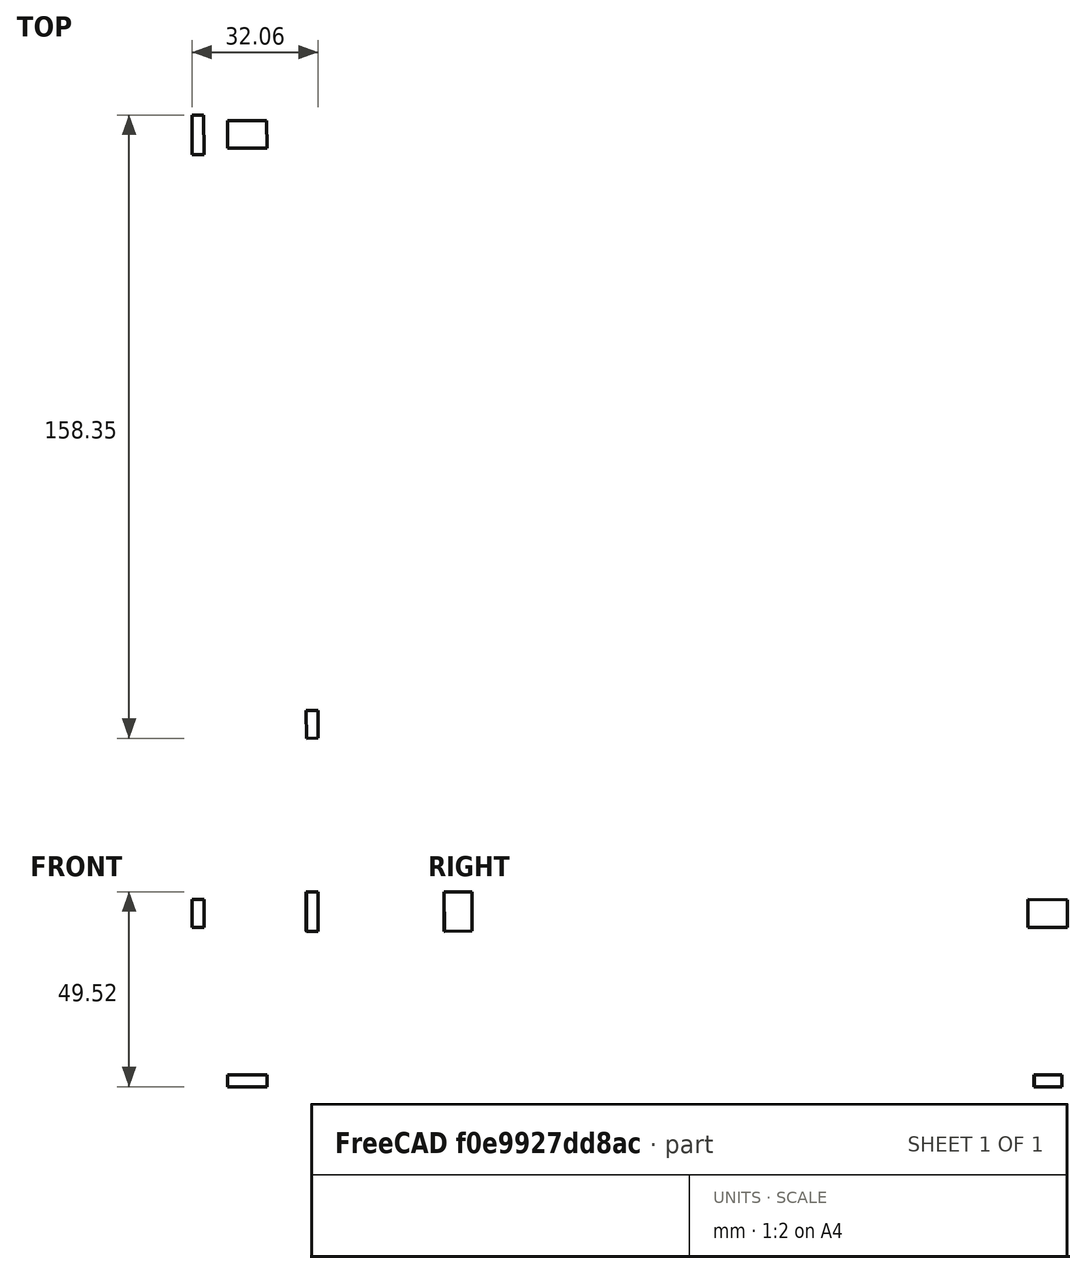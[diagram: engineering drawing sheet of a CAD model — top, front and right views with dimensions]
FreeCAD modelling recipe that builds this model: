
FCSTD DOCUMENT  (FreeCAD 2024.1R35694 (Git))
Label: 3axis_robot_rotation
License: All rights reserved
LicenseURL: https://en.wikipedia.org/wiki/All_rights_reserved
objects: App::FeaturePython×17, App::Link×14, Part::FeaturePython×3, Assembly::JointGroup×1, Assembly::AssemblyObject×1
note: 3 computed .brp shape members not serialized (recipe doc carries the construction recipe); baked Part::Feature solids carry a one-line shape summary decoded from their .brp
EXTERNAL_REF file=base.FCStd obj=Part
EXTERNAL_REF file=nema17-48.FCStd obj=Part
EXTERNAL_REF file=arm0.FCStd obj=Part
EXTERNAL_REF file=arm1.FCStd obj=Part
EXTERNAL_REF file=bearing625.FCStd obj=Part
EXTERNAL_REF file=shaft0.FCStd obj=Part
EXTERNAL_REF file=shaft1.FCStd obj=Part
EXTERNAL_REF file=bevel_gear.FCStd obj=Part
EXTERNAL_REF file=arm2.FCStd obj=Part

FEATURE [App::Link] base  label="base 🔒"
  LinkedObject = -> <external base.FCStd>#Part
FEATURE [App::Link] nema17_48
  LinkPlacement = pos=(0,0,2) rot=(0,0,1;0rad)
  LinkedObject = -> <external nema17-48.FCStd>#Part
  Placement = pos=(0,0,2) rot=(0,0,1;0rad)
FEATURE [App::Link] arm0
  LinkPlacement = pos=(-1.3e-15,-1e-16,6) rot=(0,0,1;0.006716rad)
  LinkedObject = -> <external arm0.FCStd>#Part
  Placement = pos=(-1.3e-15,-1e-16,6) rot=(0,0,1;0.006716rad)
FEATURE [App::Link] nema17_049  label="nema17_48_1"
  LinkPlacement = pos=(12.9997,0.0873078,70) rot=(0.574765,0.578638,-0.578638;4.18491rad)
  LinkedObject = -> <external nema17-48.FCStd>#Part
  Placement = pos=(12.9997,0.0873078,70) rot=(0.574765,0.578638,-0.578638;4.18491rad)
FEATURE [App::Link] arm1
  LinkPlacement = pos=(8.9998,0.0604439,70) rot=(-0.575429,-0.577323,0.579293;2.10026rad)
  LinkedObject = -> <external arm1.FCStd>#Part
  Placement = pos=(8.9998,0.0604439,70) rot=(-0.575429,-0.577323,0.579293;2.10026rad)
FEATURE [App::Link] nema17_050  label="nema17_48_2"
  LinkPlacement = pos=(-23.0868,12.8452,69.9554) rot=(0.575397,0.579274,-0.577374;2.08853rad)
  LinkedObject = -> <external nema17-48.FCStd>#Part
  Placement = pos=(-23.0868,12.8452,69.9554) rot=(0.575397,0.579274,-0.577374;2.08853rad)
FEATURE [App::Link] b625
  LinkPlacement = pos=(5.0073,-149.969,70.5145) rot=(-0.45482,-0.001527,0.890582;0.007541rad)
  LinkedObject = -> <external bearing625.FCStd>#Part
  Placement = pos=(5.0073,-149.969,70.5145) rot=(-0.45482,-0.001527,0.890582;0.007541rad)
FEATURE [App::Link] b626  label="b625_2"
  LinkPlacement = pos=(0.00741419,-150.002,70.5145) rot=(0.00237,-0.705891,0.708316;3.14635rad)
  LinkedObject = -> <external bearing625.FCStd>#Part
  Placement = pos=(0.00741419,-150.002,70.5145) rot=(0.00237,-0.705891,0.708316;3.14635rad)
FEATURE [App::Link] b627  label="b625_3"
  LinkPlacement = pos=(-22.16,-125.151,70.4287) rot=(-0.001715,-0.001727,-0.999997;1.56408rad)
  LinkedObject = -> <external bearing625.FCStd>#Part
  Placement = pos=(-22.16,-125.151,70.4287) rot=(-0.001715,-0.001727,-0.999997;1.56408rad)
FEATURE [App::Link] shaft001  label="shaft0"
  LinkPlacement = pos=(-22.066,-139.151,70.4768) rot=(0.582023,-0.576162,0.573835;4.18633rad)
  LinkedObject = -> <external shaft0.FCStd>#Part
  Placement = pos=(-22.066,-139.151,70.4768) rot=(0.582023,-0.576162,0.573835;4.18633rad)
FEATURE [App::Link] shaft1
  LinkPlacement = pos=(-3.9925,-150.029,70.5145) rot=(-0.002376,0.707591,-0.706618;3.13685rad)
  LinkedObject = -> <external shaft1.FCStd>#Part
  Placement = pos=(-3.9925,-150.029,70.5145) rot=(-0.002376,0.707591,-0.706618;3.13685rad)
FEATURE [App::Link] bevel_gear
  LinkPlacement = pos=(-3.9925,-150.029,70.5145) rot=(-0.707102,-0.002861,0.707106;3.14537rad)
  LinkedObject = -> <external bevel_gear.FCStd>#Part
  Placement = pos=(-3.9925,-150.029,70.5145) rot=(-0.707102,-0.002861,0.707106;3.14537rad)
FEATURE [App::Link] bevel_gear001
  LinkPlacement = pos=(-22.113,-132.151,70.4528) rot=(0.5725,0.580698,-0.578822;2.09287rad)
  LinkedObject = -> <external bevel_gear.FCStd>#Part
  Placement = pos=(-22.113,-132.151,70.4528) rot=(0.5725,0.580698,-0.578822;2.09287rad)
FEATURE [App::Link] arm2
  LinkPlacement = pos=(15.0071,-149.902,70.5145) rot=(-0.707102,-0.002861,0.707106;3.14537rad)
  LinkedObject = -> <external arm2.FCStd>#Part
  Placement = pos=(15.0071,-149.902,70.5145) rot=(-0.707102,-0.002861,0.707106;3.14537rad)
FEATURE [App::FeaturePython] GroundedJoint  # Assembly grounded joint (typed FeaturePython)
  ObjectToGround = -> base
FEATURE [App::FeaturePython] Fixed  # Assembly joint (typed FeaturePython)
  Activated = true
  Detach1 = false
  Detach2 = false
  Distance = 0
  Element1 = Edge11
  Element2 = Edge75
  JointType = 0 (Fixed)
  Object1 = Body
  Object2 = Body
  Offset = (0,0,0)
  Part1 = -> nema17_48
  Part2 = -> base
  Placement1 = pos=(0,0,48) rot=(0,0,1;0rad)
  Rotation = 0
  Vertex1 = Edge11
  Vertex2 = Edge75
FEATURE [App::FeaturePython] Revolute  # Assembly joint (typed FeaturePython)
  Activated = true
  Detach1 = false
  Detach2 = false
  Distance = 0
  Element1 = Face22
  Element2 = Face23
  JointType = 1 (Revolute)
  Object1 = Body
  Object2 = Body
  Offset = (0,0,0)
  Part1 = -> arm0
  Part2 = -> nema17_48
  Placement1 = pos=(4e-16,-1e-16,18) rot=(0,0,1;0rad)
  Placement2 = pos=(-9e-16,-2e-16,72) rot=(0,0,1;0rad)
  Rotation = 0
  Vertex1 = Face22
  Vertex2 = Face23
FEATURE [App::FeaturePython] Fixed001  # Assembly joint (typed FeaturePython)
  Activated = true
  Detach1 = false
  Detach2 = false
  Distance = 0
  Element1 = Edge34
  Element2 = Edge11
  JointType = 0 (Fixed)
  Object1 = Body
  Object2 = Body
  Offset = (0,0,0)
  Part1 = -> arm0
  Part2 = -> nema17_049
  Placement1 = pos=(15,5.2e-15,64) rot=(0.57735,0.57735,0.57735;2.0944rad)
  Placement2 = pos=(0,0,48) rot=(0,0,1;0rad)
  Rotation = 0
  Vertex1 = Edge34
  Vertex2 = Edge11
FEATURE [App::FeaturePython] Revolute001  # Assembly joint (typed FeaturePython)
  Activated = true
  Detach1 = false
  Detach2 = false
  Distance = 0
  Element1 = Face27
  Element2 = Face23
  JointType = 1 (Revolute)
  Object1 = Body001
  Object2 = Body
  Offset = (0,0,0)
  Part1 = -> arm1
  Part2 = -> nema17_049
  Placement1 = pos=(4e-16,-1e-16,18) rot=(0,0,1;0rad)
  Placement2 = pos=(-9e-16,-2e-16,72) rot=(0,0,1;0rad)
  Rotation = 0
  Vertex1 = Face27
  Vertex2 = Face23
FEATURE [App::FeaturePython] Fixed002  # Assembly joint (typed FeaturePython)
  Activated = true
  Detach1 = false
  Detach2 = false
  Distance = 0
  Element1 = Edge25
  Element2 = Edge11
  JointType = 0 (Fixed)
  Object1 = Body001
  Object2 = Body
  Offset = (0,0,0)
  Part1 = -> arm1
  Part2 = -> nema17_050
  Placement1 = pos=(15,-1.2e-15,32) rot=(0.57735,0.57735,0.57735;2.0944rad)
  Placement2 = pos=(0,0,48) rot=(0,0,1;0rad)
  Rotation = 0
  Vertex1 = Edge25
  Vertex2 = Edge11
FEATURE [App::FeaturePython] Fixed003  # Assembly joint (typed FeaturePython)
  Activated = true
  Detach1 = false
  Detach2 = false
  Distance = 0
  Element1 = Edge2
  Element2 = Edge81
  JointType = 0 (Fixed)
  Object1 = Body
  Object2 = Body001
  Offset = (0,0,0)
  Part1 = -> b627
  Part2 = -> arm1
  Placement2 = pos=(-125,-1.2e-15,32) rot=(0.57735,0.57735,0.57735;2.0944rad)
  Rotation = 0
  Vertex1 = Edge2
  Vertex2 = Edge81
FEATURE [App::FeaturePython] Fixed004  # Assembly joint (typed FeaturePython)
  Activated = true
  Detach1 = false
  Detach2 = false
  Distance = 0
  Element1 = Edge2
  Element2 = Edge52
  JointType = 0 (Fixed)
  Object1 = Body
  Object2 = Body001
  Offset = (0,0,0)
  Part1 = -> b626
  Part2 = -> arm1
  Placement2 = pos=(-150,-4.1e-15,10) rot=(1,0,0;3.14159rad)
  Rotation = 0
  Vertex1 = Edge2
  Vertex2 = Edge52
FEATURE [App::FeaturePython] Fixed005  # Assembly joint (typed FeaturePython)
  Activated = true
  Detach1 = false
  Detach2 = false
  Distance = 0
  Element1 = Edge3
  Element2 = Edge17
  JointType = 0 (Fixed)
  Object1 = Body
  Object2 = Body001
  Offset = (0,0,0)
  Part1 = -> b625
  Part2 = -> arm1
  Placement1 = pos=(0,0,5) rot=(0,0,1;0rad)
  Placement2 = pos=(-150,-4.1e-15,0) rot=(1,0,0;3.14159rad)
  Rotation = 0
  Vertex1 = Edge3
  Vertex2 = Edge17
FEATURE [App::FeaturePython] Revolute002  # Assembly joint (typed FeaturePython)
  Activated = true
  Detach1 = false
  Detach2 = false
  Distance = 0
  Element1 = Face11
  Element2 = Face23
  JointType = 1 (Revolute)
  Object1 = Body
  Object2 = Body
  Offset = (0,0,0)
  Part1 = -> shaft001
  Part2 = -> nema17_050
  Placement1 = pos=(-130,0,0) rot=(0.57735,0.57735,0.57735;2.0944rad)
  Placement2 = pos=(0,0,72) rot=(0,0,1;0rad)
  Rotation = 0
  Vertex1 = Edge1
  Vertex2 = Edge1
FEATURE [App::FeaturePython] Revolute003  # Assembly joint (typed FeaturePython)
  Activated = true
  Detach1 = false
  Detach2 = false
  Distance = 0
  Element1 = Edge2
  Element2 = Edge5
  JointType = 1 (Revolute)
  Object1 = Body
  Object2 = Body
  Offset = (0,0,0)
  Part1 = -> shaft1
  Part2 = -> b626
  Placement1 = pos=(-4,0,0) rot=(0.57735,0.57735,0.57735;2.0944rad)
  Rotation = 0
  Vertex1 = Edge2
  Vertex2 = Edge5
FEATURE [App::FeaturePython] Fixed006  # Assembly joint (typed FeaturePython)
  Activated = true
  Detach1 = false
  Detach2 = false
  Distance = 0
  Element1 = Face4
  Element2 = Edge3
  JointType = 0 (Fixed)
  Object1 = Body
  Object2 = Body
  Offset = (0,0,0)
  Part1 = -> shaft1
  Part2 = -> arm2
  Placement1 = pos=(-19,0,0) rot=(0.57735,0.57735,0.57735;2.0944rad)
  Rotation = 0
  Vertex1 = Edge1
  Vertex2 = Edge3
FEATURE [App::FeaturePython] Fixed007  # Assembly joint (typed FeaturePython)
  Activated = true
  Detach1 = false
  Detach2 = false
  Distance = 0
  Element2 = Edge5
  JointType = 0 (Fixed)
  Object1 = Body
  Object2 = Body
  Offset = (0,0,0)
  Part1 = -> bevel_gear
  Part2 = -> shaft1
  Placement2 = pos=(0,0,0) rot=(0.57735,0.57735,0.57735;2.0944rad)
  Rotation = 0
  Vertex2 = Edge5
FEATURE [App::FeaturePython] Fixed008  # Assembly joint (typed FeaturePython)
  Activated = true
  Detach1 = false
  Detach2 = false
  Distance = 0
  Element2 = Edge9
  JointType = 0 (Fixed)
  Object1 = Body
  Object2 = Body
  Offset = (0,0,0)
  Part1 = -> bevel_gear001
  Part2 = -> shaft001
  Placement2 = pos=(-7,0,0) rot=(-0.57735,-0.57735,0.57735;2.0944rad)
  Rotation = 0
  Vertex2 = Edge9
FEATURE [Part::FeaturePython] MotorObserver0  # WARN: FeaturePython — macro-defined, semantics opaque (R4)
  Enabled = true
  Placement = pos=(-1.5e-15,-1e-16,27.5) rot=(0,0,1;0.006716rad)
  SupportObject = -> nema17_48
  TransfAngle = 0
FEATURE [Part::FeaturePython] MotorObserver1  # WARN: FeaturePython — macro-defined, semantics opaque (R4)
  Enabled = true
  Placement = pos=(-12.4997,-0.0839498,70) rot=(-0.575429,-0.577323,0.579293;2.10026rad)
  SupportObject = -> nema17_049
  TransfAngle = 0
FEATURE [Part::FeaturePython] MotorObserver2  # WARN: FeaturePython — macro-defined, semantics opaque (R4)
  Enabled = true
  Placement = pos=(16.507,-149.892,70.5145) rot=(-0.00267,0.999988,0.004046;1.57081rad)
  SupportObject = -> arm1
  TransfAngle = 0
FEATURE [App::FeaturePython] Fixed009  # Assembly joint (typed FeaturePython)
  Activated = true
  Detach1 = false
  Detach2 = false
  Distance = 0
  Element1 = Face5
  Element2 = Edge4
  JointType = 0 (Fixed)
  Object1 = MotorObserver0
  Object2 = Body
  Offset = (0,0,0)
  Part1 = -> MotorObserver0
  Part2 = -> arm0
  Placement1 = pos=(1e-16,0,-1.5) rot=(0,0,1;0rad)
  Placement2 = pos=(0,0,20) rot=(0,0,1;0rad)
  Rotation = 0
  Vertex1 = Face5
  Vertex2 = Edge4
FEATURE [App::FeaturePython] Fixed010  # Assembly joint (typed FeaturePython)
  Activated = true
  Detach1 = false
  Detach2 = false
  Distance = 0
  Element1 = Face5
  Element2 = Edge47
  JointType = 0 (Fixed)
  Object1 = MotorObserver1
  Object2 = Body001
  Offset = (0,0,0)
  Part1 = -> MotorObserver1
  Part2 = -> arm1
  Placement1 = pos=(2e-16,0,-1.5) rot=(0,0,1;0rad)
  Placement2 = pos=(0,0,20) rot=(0,0,1;0rad)
  Rotation = 0
  Vertex1 = Face5
  Vertex2 = Edge47
FEATURE [App::FeaturePython] Fixed011  # Assembly joint (typed FeaturePython)
  Activated = true
  Detach1 = false
  Detach2 = false
  Distance = 0
  Element1 = Face5
  Element2 = Edge3
  JointType = 0 (Fixed)
  Object1 = MotorObserver2
  Object2 = Body
  Offset = (0,0,0)
  Part1 = -> MotorObserver2
  Part2 = -> arm2
  Placement1 = pos=(0,2.84e-14,-1.5) rot=(0,0,1;0rad)
  Rotation = 0
  Vertex1 = Face5
  Vertex2 = Edge3
FEATURE [Assembly::JointGroup] Joints
  Group = -> [GroundedJoint,Fixed,Revolute,Fixed001,Revolute001,Fixed002,Fixed003,Fixed004,Fixed005,Revolute002,Revolute003,Fixed006,Fixed007,Fixed008,Fixed009,Fixed010,Fixed011]
FEATURE [Assembly::AssemblyObject] Assembly  label="3axis_robot"
  Group = -> [Joints,base,nema17_48,arm0,nema17_049,arm1,nema17_050,b625,b626,b627,shaft001,shaft1,bevel_gear,bevel_gear001,arm2,GroundedJoint,Fixed,Revolute,Fixed001,Revolute001,Fixed002,Fixed003,Fixed004,Fixed005,Revolute002,Revolute003,Fixed006,Fixed007,Fixed008,MotorObserver0,MotorObserver1,MotorObserver2,Fixed009,Fixed010,Fixed011]
  Origin = -> Origin
  Type = Assembly

RESOLVED EXTERNAL PARTS (link-assembly join: the EXTERNAL_REF files above that resolve inside this repo's crawl, each included once):
---- part arm0.FCStd = doc fcstd_8672410c447e ----
FCSTD DOCUMENT  (FreeCAD 2024.1R35694 (Git))
Label: arm0
License: All rights reserved
LicenseURL: https://en.wikipedia.org/wiki/All_rights_reserved
objects: Sketcher::SketchObject×11, PartDesign::Pad×6, PartDesign::Hole×3, PartDesign::Body×2, PartDesign::Pocket×2, PartDesign::Fillet×1, App::Part×1
note: 37 computed .brp shape members not serialized (recipe doc carries the construction recipe); baked Part::Feature solids carry a one-line shape summary decoded from their .brp

FEATURE [Sketcher::SketchObject] Sketch
  FullyConstrained = true
  MapMode = 5
  Support = -> [XY_Plane001]
  sketch-geometry (5):
    g0: Circle CenterX=0 CenterY=0 CenterZ=0 NormalX=0 NormalY=0 NormalZ=1 AngleXU=0 Radius=2.5
    g1: ArcOfCircle CenterX=0 CenterY=0 CenterZ=0 NormalX=0 NormalY=0 NormalZ=1 AngleXU=0 Radius=7.5 StartAngle=1.5708 EndAngle=4.71239
    g2: LineSegment StartX=-1.2e-15 StartY=7.5 StartZ=0 EndX=15 EndY=7.5 EndZ=0
    g3: LineSegment StartX=15 StartY=7.5 StartZ=0 EndX=15 EndY=-7.5 EndZ=0
    g4: LineSegment StartX=15 StartY=-7.5 StartZ=0 EndX=1.8e-15 EndY=-7.5 EndZ=0
  constraints (12):
    c: Coincident(g0,g-1)
    c: Coincident(g1,g0)
    c: Diameter(g0) = 5
    c: Diameter(g1) = 15
    c: Horizontal(g2)
    c: Coincident(g2,g3)
    c: Vertical(g3)
    c: Coincident(g3,g4)
    c: Horizontal(g4)
    c: Tangent(g1,g4) = 1.5708
    c: Tangent(g1,g2) = 1.5708
    c: DistanceX(g2,g2) = 15
FEATURE [PartDesign::Pad] Pad
  Direction = (0,0,1)
  Length = 20
  Length2 = 10
  Profile = -> Sketch
  ReferenceAxis = -> Sketch [N_Axis]
  Refine = true
  Type = 0
FEATURE [Sketcher::SketchObject] Sketch001
  ExternalGeometry = -> [Pad]
  FullyConstrained = true
  MapMode = 5
  Placement = pos=(15,0,0) rot=(0.57735,0.57735,0.57735;2.0944rad)
  Support = -> [Pad]
  sketch-geometry (8):
    g0: LineSegment StartX=-7.5 StartY=0 StartZ=0 EndX=-21 EndY=43 EndZ=0
    g1: LineSegment StartX=-21 StartY=43 StartZ=0 EndX=-21 EndY=85 EndZ=0
    g2: LineSegment StartX=-21 StartY=85 StartZ=0 EndX=21 EndY=85 EndZ=0
    g3: LineSegment StartX=21 StartY=85 StartZ=0 EndX=21 EndY=43 EndZ=0
    g4: LineSegment StartX=21 StartY=43 StartZ=0 EndX=7.5 EndY=0 EndZ=0
    g5: LineSegment StartX=7.5 StartY=0 StartZ=0 EndX=-7.5 EndY=0 EndZ=0
    g6: GeomPoint X=5.2e-15 Y=64 Z=0
    g7: Circle CenterX=5.2e-15 CenterY=64 CenterZ=0 NormalX=0 NormalY=0 NormalZ=1 AngleXU=0 Radius=11.25
  constraints (18):
    c: PointOnObject(g0,g-1)
    c: Coincident(g0,g1)
    c: Vertical(g1)
    c: Coincident(g1,g2)
    c: Coincident(g2,g3)
    c: Coincident(g3,g4)
    c: Coincident(g4,g5)
    c: Coincident(g5,g0)
    c: Symmetric(g0,g3,g-2)
    c: Symmetric(g1,g2,g-2)
    c: DistanceX(g2,g2) = 42
    c: DistanceY(g3,g3) = 42
    c: Symmetric(g0,g4,g-2)
    c: DistanceX(g5,g5) = 15
    c: Symmetric(g1,g3,g6)
    c: Coincident(g7,g6)
    c: Diameter(g7) = 22.5
    c: DistanceY(g-1,g3) = 43
FEATURE [PartDesign::Pad] Pad001
  BaseFeature = -> Pad
  Direction = (1,0,0)
  Length = 4
  Length2 = 10
  Profile = -> Sketch001
  ReferenceAxis = -> Sketch001 [N_Axis]
  Refine = true
  Reversed = true
  Type = 0
FEATURE [Sketcher::SketchObject] Sketch003
  ExternalGeometry = -> [Pad001]
  FullyConstrained = true
  MapMode = 5
  Placement = pos=(11,0,0) rot=(0.57735,-0.57735,-0.57735;2.0944rad)
  Support = -> [Pad001]
  sketch-geometry (5):
    g0: Circle CenterX=15.5 CenterY=79.5 CenterZ=0 NormalX=0 NormalY=0 NormalZ=1 AngleXU=0 Radius=1.5
    g1: LineSegment StartX=-5.2e-15 StartY=64 StartZ=0 EndX=11.25 EndY=64 EndZ=0
    g2: Circle CenterX=-15.5 CenterY=79.5 CenterZ=0 NormalX=0 NormalY=0 NormalZ=1 AngleXU=0 Radius=1.5
    g3: Circle CenterX=15.5 CenterY=48.5 CenterZ=0 NormalX=0 NormalY=0 NormalZ=1 AngleXU=0 Radius=1.5
    g4: Circle CenterX=-15.5 CenterY=48.5 CenterZ=0 NormalX=0 NormalY=0 NormalZ=1 AngleXU=0 Radius=1.5
  constraints (12):
    c: DistanceY(g-3,g0) = 15.5
    c: DistanceX(g-3,g0) = 15.5
    c: Diameter(g0) = 3
    c: Coincident(g1,g-3)
    c: Horizontal(g1)
    c: PointOnObject(g1,g-3)
    c: Diameter(g2) = 3
    c: Diameter(g3) = 3
    c: Diameter(g4) = 3
    c: Symmetric(g2,g0,g-2)
    c: Symmetric(g4,g3,g-2)
    c: Symmetric(g3,g0,g1)
FEATURE [PartDesign::Hole] Hole
  BaseFeature = -> Pad001
  CustomThreadClearance = 0
  Depth = 25
  DepthType = 0
  Diameter = 3.4
  DrillForDepth = false
  DrillPoint = 1
  DrillPointAngle = 118
  HoleCutCountersinkAngle = 90
  HoleCutCustomValues = false
  HoleCutDepth = 2
  HoleCutDiameter = 6.1
  HoleCutType = 1
  ModelThread = false
  Profile = -> Sketch003
  Refine = true
  Tapered = false
  TaperedAngle = 90
  ThreadClass = 0
  ThreadDepth = 25
  ThreadDepthType = 0
  ThreadDirection = 0
  ThreadFit = 0
  ThreadSize = 9
  ThreadType = 1
  Threaded = false
  UseCustomThreadClearance = false
FEATURE [Sketcher::SketchObject] Sketch004
  ExternalGeometry = -> [Hole]
  FullyConstrained = true
  MapMode = 5
  Placement = pos=(0,0,20) rot=(0,0,1;0rad)
  Support = -> [Hole]
  sketch-geometry (1):
    g0: Circle CenterX=0 CenterY=0 CenterZ=0 NormalX=0 NormalY=0 NormalZ=1 AngleXU=0 Radius=2.5
  constraints (2):
    c: Coincident(g0,g-3)
    c: Equal(g0,g-3)
FEATURE [PartDesign::Pad] Pad002
  BaseFeature = -> Hole
  Direction = (0,0,1)
  Length = 2
  Length2 = 10
  Profile = -> Sketch004
  ReferenceAxis = -> Sketch004 [N_Axis]
  Refine = true
  Reversed = true
  Type = 0
FEATURE [PartDesign::Body] Body  label="arm0-skel"
  Group = -> [Sketch,Pad,Sketch001,Pad001,Sketch003,Hole,Sketch004,Pad002]
  Origin = -> Origin001
  Tip = -> Pad002
FEATURE [Sketcher::SketchObject] Sketch008
  FullyConstrained = true
  MapMode = 5
  Support = -> [XY_Plane002]
  sketch-geometry (5):
    g0: Circle CenterX=0 CenterY=0 CenterZ=0 NormalX=0 NormalY=0 NormalZ=1 AngleXU=0 Radius=2.5
    g1: ArcOfCircle CenterX=0 CenterY=0 CenterZ=0 NormalX=0 NormalY=0 NormalZ=1 AngleXU=0 Radius=7.5 StartAngle=1.5708 EndAngle=4.71239
    g2: LineSegment StartX=-1.2e-15 StartY=7.5 StartZ=0 EndX=15 EndY=7.5 EndZ=0
    g3: LineSegment StartX=15 StartY=7.5 StartZ=0 EndX=15 EndY=-7.5 EndZ=0
    g4: LineSegment StartX=15 StartY=-7.5 StartZ=0 EndX=1.8e-15 EndY=-7.5 EndZ=0
  constraints (12):
    c: Coincident(g0,g-1)
    c: Coincident(g1,g0)
    c: Diameter(g0) = 5
    c: Diameter(g1) = 15
    c: Horizontal(g2)
    c: Coincident(g2,g3)
    c: Vertical(g3)
    c: Coincident(g3,g4)
    c: Horizontal(g4)
    c: Tangent(g1,g4) = 1.5708
    c: Tangent(g1,g2) = 1.5708
    c: DistanceX(g2,g2) = 15
FEATURE [PartDesign::Pad] Pad003
  Direction = (0,0,1)
  Length = 20
  Length2 = 10
  Profile = -> Sketch008
  ReferenceAxis = -> Sketch008 [N_Axis]
  Refine = true
  Type = 0
FEATURE [Sketcher::SketchObject] Sketch009
  ExternalGeometry = -> [Pad003]
  FullyConstrained = true
  MapMode = 5
  Placement = pos=(15,0,0) rot=(0.57735,0.57735,0.57735;2.0944rad)
  Support = -> [Pad003]
  sketch-geometry (8):
    g0: LineSegment StartX=-7.5 StartY=0 StartZ=0 EndX=-21 EndY=43 EndZ=0
    g1: LineSegment StartX=-21 StartY=43 StartZ=0 EndX=-21 EndY=85 EndZ=0
    g2: LineSegment StartX=-21 StartY=85 StartZ=0 EndX=21 EndY=85 EndZ=0
    g3: LineSegment StartX=21 StartY=85 StartZ=0 EndX=21 EndY=43 EndZ=0
    g4: LineSegment StartX=21 StartY=43 StartZ=0 EndX=7.5 EndY=0 EndZ=0
    g5: LineSegment StartX=7.5 StartY=0 StartZ=0 EndX=-7.5 EndY=0 EndZ=0
    g6: GeomPoint X=4.8e-15 Y=64 Z=0
    g7: Circle CenterX=4.8e-15 CenterY=64 CenterZ=0 NormalX=0 NormalY=0 NormalZ=1 AngleXU=0 Radius=11.25
  constraints (18):
    c: PointOnObject(g0,g-1)
    c: Coincident(g0,g1)
    c: Vertical(g1)
    c: Coincident(g1,g2)
    c: Coincident(g2,g3)
    c: Coincident(g3,g4)
    c: Coincident(g4,g5)
    c: Coincident(g5,g0)
    c: Symmetric(g0,g3,g-2)
    c: Symmetric(g1,g2,g-2)
    c: DistanceX(g2,g2) = 42
    c: DistanceY(g3,g3) = 42
    c: Symmetric(g0,g4,g-2)
    c: DistanceX(g5,g5) = 15
    c: Symmetric(g1,g3,g6)
    c: Coincident(g7,g6)
    c: Diameter(g7) = 22.5
    c: DistanceY(g-1,g3) = 43
FEATURE [PartDesign::Pad] Pad004
  BaseFeature = -> Pad003
  Direction = (1,0,0)
  Length = 4
  Length2 = 10
  Profile = -> Sketch009
  ReferenceAxis = -> Sketch009 [N_Axis]
  Refine = true
  Reversed = true
  Type = 0
FEATURE [Sketcher::SketchObject] Sketch010
  ExternalGeometry = -> [Pad004]
  FullyConstrained = true
  MapMode = 5
  Placement = pos=(11,0,0) rot=(0.57735,-0.57735,-0.57735;2.0944rad)
  Support = -> [Pad004]
  sketch-geometry (5):
    g0: Circle CenterX=15.5 CenterY=79.5 CenterZ=0 NormalX=0 NormalY=0 NormalZ=1 AngleXU=0 Radius=1.5
    g1: LineSegment StartX=-4.8e-15 StartY=64 StartZ=0 EndX=11.25 EndY=64 EndZ=0
    g2: Circle CenterX=-15.5 CenterY=79.5 CenterZ=0 NormalX=0 NormalY=0 NormalZ=1 AngleXU=0 Radius=1.5
    g3: Circle CenterX=15.5 CenterY=48.5 CenterZ=0 NormalX=0 NormalY=0 NormalZ=1 AngleXU=0 Radius=1.5
    g4: Circle CenterX=-15.5 CenterY=48.5 CenterZ=0 NormalX=0 NormalY=0 NormalZ=1 AngleXU=0 Radius=1.5
  constraints (12):
    c: DistanceY(g-3,g0) = 15.5
    c: DistanceX(g-3,g0) = 15.5
    c: Diameter(g0) = 3
    c: Coincident(g1,g-3)
    c: Horizontal(g1)
    c: PointOnObject(g1,g-3)
    c: Diameter(g2) = 3
    c: Diameter(g3) = 3
    c: Diameter(g4) = 3
    c: Symmetric(g2,g0,g-2)
    c: Symmetric(g4,g3,g-2)
    c: Symmetric(g3,g0,g1)
FEATURE [PartDesign::Hole] Hole002
  BaseFeature = -> Pad004
  CustomThreadClearance = 0
  Depth = 25
  DepthType = 0
  Diameter = 3.4
  DrillForDepth = false
  DrillPoint = 1
  DrillPointAngle = 118
  HoleCutCountersinkAngle = 90
  HoleCutCustomValues = false
  HoleCutDepth = 2
  HoleCutDiameter = 6.1
  HoleCutType = 1
  ModelThread = false
  Profile = -> Sketch010
  Refine = true
  Tapered = false
  TaperedAngle = 90
  ThreadClass = 0
  ThreadDepth = 25
  ThreadDepthType = 0
  ThreadDirection = 0
  ThreadFit = 0
  ThreadSize = 9
  ThreadType = 1
  Threaded = false
  UseCustomThreadClearance = false
FEATURE [Sketcher::SketchObject] Sketch011
  ExternalGeometry = -> [Hole002]
  FullyConstrained = true
  MapMode = 5
  Placement = pos=(0,0,20) rot=(0,0,1;0rad)
  Support = -> [Hole002]
  sketch-geometry (1):
    g0: Circle CenterX=0 CenterY=0 CenterZ=0 NormalX=0 NormalY=0 NormalZ=1 AngleXU=0 Radius=2.5
  constraints (2):
    c: Coincident(g0,g-3)
    c: Equal(g0,g-3)
FEATURE [PartDesign::Pad] Pad005
  BaseFeature = -> Hole002
  Direction = (0,0,1)
  Length = 2
  Length2 = 10
  Profile = -> Sketch011
  ReferenceAxis = -> Sketch011 [N_Axis]
  Refine = true
  Reversed = true
  Type = 0
FEATURE [Sketcher::SketchObject] Sketch012
  FullyConstrained = true
  MapMode = 5
  Placement = pos=(0,0,0) rot=(1,0,0;3.14159rad)
  Support = -> [Pad005]
  sketch-geometry (4):
    g0: LineSegment StartX=0 StartY=1 StartZ=0 EndX=0 EndY=-1 EndZ=0
    g1: LineSegment StartX=0 StartY=-1 StartZ=0 EndX=10 EndY=-1 EndZ=0
    g2: LineSegment StartX=10 StartY=-1 StartZ=0 EndX=10 EndY=1 EndZ=0
    g3: LineSegment StartX=10 StartY=1 StartZ=0 EndX=0 EndY=1 EndZ=0
  constraints (11):
    c: Coincident(g0,g1)
    c: Coincident(g1,g2)
    c: Coincident(g2,g3)
    c: Coincident(g3,g0)
    c: Vertical(g0)
    c: Horizontal(g1)
    c: Horizontal(g3)
    c: PointOnObject(g0,g-2)
    c: Symmetric(g1,g2,g-1)
    c: DistanceY(g2,g2) = 2
    c: DistanceX(g3,g3) = 10
FEATURE [PartDesign::Pocket] Pocket002
  BaseFeature = -> Pad005
  Direction = (0,0,1)
  Length = 5
  Length2 = 5
  Profile = -> Sketch012
  ReferenceAxis = -> Sketch012 [N_Axis]
  Refine = true
  Type = 1
FEATURE [Sketcher::SketchObject] Sketch013
  FullyConstrained = true
  MapMode = 5
  Placement = pos=(0,-7.5,0) rot=(1,0,0;1.5708rad)
  Support = -> [Pocket002]
  sketch-geometry (1):
    g0: Circle CenterX=6 CenterY=10 CenterZ=0 NormalX=0 NormalY=0 NormalZ=1 AngleXU=0 Radius=1.5
  constraints (3):
    c: DistanceY(g-1,g0) = 10
    c: DistanceX(g-1,g0) = 6
    c: Diameter(g0) = 3
FEATURE [PartDesign::Hole] Hole003
  BaseFeature = -> Pocket002
  CustomThreadClearance = 0
  Depth = 25
  DepthType = 0
  Diameter = 4.5
  DrillForDepth = false
  DrillPoint = 1
  DrillPointAngle = 118
  HoleCutCountersinkAngle = 90
  HoleCutCustomValues = false
  HoleCutDepth = 0
  HoleCutDiameter = 6.1
  HoleCutType = 0
  ModelThread = false
  Profile = -> Sketch013
  Refine = true
  Tapered = false
  TaperedAngle = 90
  ThreadClass = 0
  ThreadDepth = 25
  ThreadDepthType = 0
  ThreadDirection = 0
  ThreadFit = 0
  ThreadSize = 11
  ThreadType = 1
  Threaded = false
  UseCustomThreadClearance = false
FEATURE [Sketcher::SketchObject] Sketch014
  ExternalGeometry = -> [Hole003]
  FullyConstrained = true
  MapMode = 5
  Placement = pos=(0,7.5,0) rot=(0,0.707107,0.707107;3.14159rad)
  Support = -> [Hole003]
  sketch-geometry (7):
    g0: LineSegment StartX=-1.95855 StartY=10 StartZ=0 EndX=-3.97927 EndY=13.5 EndZ=0
    g1: LineSegment StartX=-3.97927 StartY=13.5 StartZ=0 EndX=-8.02073 EndY=13.5 EndZ=0
    g2: LineSegment StartX=-8.02073 StartY=13.5 StartZ=0 EndX=-10.0415 EndY=10 EndZ=0
    g3: LineSegment StartX=-10.0415 StartY=10 StartZ=0 EndX=-8.02073 EndY=6.5 EndZ=0
    g4: LineSegment StartX=-8.02073 StartY=6.5 StartZ=0 EndX=-3.97927 EndY=6.5 EndZ=0
    g5: LineSegment StartX=-3.97927 StartY=6.5 StartZ=0 EndX=-1.95855 EndY=10 EndZ=0
    g6: Circle CenterX=-6 CenterY=10 CenterZ=0 NormalX=0 NormalY=0 NormalZ=1 AngleXU=0 Radius=4.04145
  constraints (16):
    c: Coincident(g0,g1)
    c: Coincident(g1,g2)
    c: Coincident(g2,g3)
    c: Coincident(g3,g4)
    c: Coincident(g4,g5)
    c: Coincident(g5,g0)
    c: Equal(g0, g1-g5) x5
    c: PointOnObject(g0,g6)
    c: PointOnObject(g1,g6)
    c: PointOnObject(g2,g6)
    c: PointOnObject(g3,g6)
    c: PointOnObject(g4,g6)
    c: PointOnObject(g5,g6)
    c: Coincident(g6,g-3)
    c: Horizontal(g1)
    c: DistanceY(g4,g0) = 7
FEATURE [PartDesign::Pocket] Pocket003
  BaseFeature = -> Hole003
  Direction = (0,-1,2e-16)
  Length = 4
  Length2 = 5
  Profile = -> Sketch014
  ReferenceAxis = -> Sketch014 [N_Axis]
  Refine = true
  Type = 0
FEATURE [PartDesign::Fillet] Fillet
  Base = -> Pocket003 [Edge77,Edge78,Edge65,Edge54]
  BaseFeature = -> Pocket003
  Radius = 6
  Refine = true
  SupportTransform = false
  UseAllEdges = false
FEATURE [PartDesign::Body] Body001  label="arm0s"
  Group = -> [Sketch008,Pad003,Sketch009,Pad004,Sketch010,Hole002,Sketch011,Pad005,Sketch012,Pocket002,Sketch013,Hole003,Sketch014,Pocket003,Fillet]
  Origin = -> Origin002
  Tip = -> Fillet
FEATURE [App::Part] Part  label="arm0"
  Group = -> [Body,Body001]
  Origin = -> Origin
---- part arm1.FCStd = doc fcstd_9c4ea4d260db ----
FCSTD DOCUMENT  (FreeCAD 2024.1R35694 (Git))
Label: arm1
License: All rights reserved
LicenseURL: https://en.wikipedia.org/wiki/All_rights_reserved
objects: Sketcher::SketchObject×17, PartDesign::Pad×11, PartDesign::Chamfer×8, PartDesign::Plane×4, PartDesign::Hole×3, PartDesign::Pocket×3, PartDesign::Body×2, PartDesign::Fillet×1, App::Part×1
note: 75 computed .brp shape members not serialized (recipe doc carries the construction recipe); baked Part::Feature solids carry a one-line shape summary decoded from their .brp

FEATURE [Sketcher::SketchObject] Sketch
  FullyConstrained = true
  MapMode = 5
  Support = -> [XY_Plane001]
  sketch-geometry (5):
    g0: Circle CenterX=0 CenterY=0 CenterZ=0 NormalX=0 NormalY=0 NormalZ=1 AngleXU=0 Radius=2.5
    g1: ArcOfCircle CenterX=0 CenterY=0 CenterZ=0 NormalX=0 NormalY=0 NormalZ=1 AngleXU=0 Radius=7.5 StartAngle=1.5708 EndAngle=4.71239
    g2: LineSegment StartX=-1.2e-15 StartY=7.5 StartZ=0 EndX=15 EndY=7.5 EndZ=0
    g3: LineSegment StartX=15 StartY=7.5 StartZ=0 EndX=15 EndY=-7.5 EndZ=0
    g4: LineSegment StartX=15 StartY=-7.5 StartZ=0 EndX=1.8e-15 EndY=-7.5 EndZ=0
  constraints (12):
    c: Coincident(g0,g-1)
    c: Coincident(g1,g0)
    c: Diameter(g0) = 5
    c: Diameter(g1) = 15
    c: Horizontal(g2)
    c: Coincident(g2,g3)
    c: Vertical(g3)
    c: Coincident(g3,g4)
    c: Horizontal(g4)
    c: Tangent(g1,g4) = 1.5708
    c: Tangent(g1,g2) = 1.5708
    c: DistanceX(g2,g2) = 15
FEATURE [PartDesign::Pad] Pad
  Direction = (0,0,1)
  Length = 20
  Length2 = 10
  Profile = -> Sketch
  ReferenceAxis = -> Sketch [N_Axis]
  Refine = true
  Type = 0
FEATURE [Sketcher::SketchObject] Sketch001
  ExternalGeometry = -> [Pad]
  FullyConstrained = true
  MapMode = 5
  Placement = pos=(15,0,0) rot=(0.57735,0.57735,0.57735;2.0944rad)
  Support = -> [Pad]
  sketch-geometry (8):
    g0: LineSegment StartX=-7.5 StartY=0 StartZ=0 EndX=-21 EndY=11 EndZ=0
    g1: LineSegment StartX=-21 StartY=11 StartZ=0 EndX=-21 EndY=53 EndZ=0
    g2: LineSegment StartX=-21 StartY=53 StartZ=0 EndX=21 EndY=53 EndZ=0
    g3: LineSegment StartX=21 StartY=53 StartZ=0 EndX=21 EndY=11 EndZ=0
    g4: LineSegment StartX=21 StartY=11 StartZ=0 EndX=7.5 EndY=0 EndZ=0
    g5: LineSegment StartX=7.5 StartY=0 StartZ=0 EndX=-7.5 EndY=0 EndZ=0
    g6: GeomPoint X=-1.2e-15 Y=32 Z=0
    g7: Circle CenterX=-1.2e-15 CenterY=32 CenterZ=0 NormalX=0 NormalY=0 NormalZ=1 AngleXU=0 Radius=11.25
  constraints (18):
    c: PointOnObject(g0,g-1)
    c: Coincident(g0,g1)
    c: Vertical(g1)
    c: Coincident(g1,g2)
    c: Coincident(g2,g3)
    c: Coincident(g3,g4)
    c: Coincident(g4,g5)
    c: Coincident(g5,g0)
    c: Symmetric(g0,g3,g-2)
    c: Symmetric(g1,g2,g-2)
    c: DistanceX(g2,g2) = 42
    c: DistanceY(g3,g3) = 42
    c: Symmetric(g0,g4,g-2)
    c: DistanceX(g5,g5) = 15
    c: Symmetric(g1,g3,g6)
    c: Coincident(g7,g6)
    c: Diameter(g7) = 22.5
    c: DistanceY(g-1,g3) = 11
FEATURE [PartDesign::Pad] Pad001
  BaseFeature = -> Pad
  Direction = (1,0,0)
  Length = 4
  Length2 = 10
  Profile = -> Sketch001
  ReferenceAxis = -> Sketch001 [N_Axis]
  Refine = true
  Reversed = true
  Type = 0
FEATURE [Sketcher::SketchObject] Sketch003
  ExternalGeometry = -> [Pad001]
  FullyConstrained = true
  MapMode = 5
  Placement = pos=(11,0,0) rot=(0.57735,-0.57735,-0.57735;2.0944rad)
  Support = -> [Pad001]
  sketch-geometry (5):
    g0: Circle CenterX=15.5 CenterY=47.5 CenterZ=0 NormalX=0 NormalY=0 NormalZ=1 AngleXU=0 Radius=1.5
    g1: LineSegment StartX=1.2e-15 StartY=32 StartZ=0 EndX=11.25 EndY=32 EndZ=0
    g2: Circle CenterX=-15.5 CenterY=47.5 CenterZ=0 NormalX=0 NormalY=0 NormalZ=1 AngleXU=0 Radius=1.5
    g3: Circle CenterX=15.5 CenterY=16.5 CenterZ=0 NormalX=0 NormalY=0 NormalZ=1 AngleXU=0 Radius=1.5
    g4: Circle CenterX=-15.5 CenterY=16.5 CenterZ=0 NormalX=0 NormalY=0 NormalZ=1 AngleXU=0 Radius=1.5
  constraints (12):
    c: DistanceY(g-3,g0) = 15.5
    c: DistanceX(g-3,g0) = 15.5
    c: Diameter(g0) = 3
    c: Coincident(g1,g-3)
    c: Horizontal(g1)
    c: PointOnObject(g1,g-3)
    c: Diameter(g2) = 3
    c: Diameter(g3) = 3
    c: Diameter(g4) = 3
    c: Symmetric(g2,g0,g-2)
    c: Symmetric(g4,g3,g-2)
    c: Symmetric(g3,g0,g1)
FEATURE [PartDesign::Hole] Hole
  BaseFeature = -> Pad001
  CustomThreadClearance = 0
  Depth = 25
  DepthType = 0
  Diameter = 3.4
  DrillForDepth = false
  DrillPoint = 1
  DrillPointAngle = 118
  HoleCutCountersinkAngle = 90
  HoleCutCustomValues = false
  HoleCutDepth = 2
  HoleCutDiameter = 6.1
  HoleCutType = 1
  ModelThread = false
  Profile = -> Sketch003
  Refine = true
  Tapered = false
  TaperedAngle = 90
  ThreadClass = 0
  ThreadDepth = 25
  ThreadDepthType = 0
  ThreadDirection = 0
  ThreadFit = 0
  ThreadSize = 9
  ThreadType = 1
  Threaded = false
  UseCustomThreadClearance = false
FEATURE [Sketcher::SketchObject] Sketch004
  ExternalGeometry = -> [Hole]
  FullyConstrained = true
  MapMode = 5
  Placement = pos=(0,0,20) rot=(0,0,1;0rad)
  Support = -> [Hole]
  sketch-geometry (1):
    g0: Circle CenterX=0 CenterY=0 CenterZ=0 NormalX=0 NormalY=0 NormalZ=1 AngleXU=0 Radius=2.5
  constraints (2):
    c: Coincident(g0,g-3)
    c: Equal(g0,g-3)
FEATURE [PartDesign::Pad] Pad002
  BaseFeature = -> Hole
  Direction = (0,0,1)
  Length = 2
  Length2 = 10
  Profile = -> Sketch004
  ReferenceAxis = -> Sketch004 [N_Axis]
  Refine = true
  Reversed = true
  Type = 0
FEATURE [Sketcher::SketchObject] Sketch005
  FullyConstrained = true
  MapMode = 5
  Placement = pos=(0,0,0) rot=(1,0,0;3.14159rad)
  Support = -> [Pad002]
  sketch-geometry (4):
    g0: LineSegment StartX=0 StartY=1 StartZ=0 EndX=0 EndY=-1 EndZ=0
    g1: LineSegment StartX=0 StartY=-1 StartZ=0 EndX=10 EndY=-1 EndZ=0
    g2: LineSegment StartX=10 StartY=-1 StartZ=0 EndX=10 EndY=1 EndZ=0
    g3: LineSegment StartX=10 StartY=1 StartZ=0 EndX=0 EndY=1 EndZ=0
  constraints (11):
    c: Coincident(g0,g1)
    c: Coincident(g1,g2)
    c: Coincident(g2,g3)
    c: Coincident(g3,g0)
    c: Vertical(g0)
    c: Horizontal(g1)
    c: Horizontal(g3)
    c: PointOnObject(g0,g-2)
    c: Symmetric(g1,g2,g-1)
    c: DistanceY(g2,g2) = 2
    c: DistanceX(g3,g3) = 10
FEATURE [PartDesign::Pocket] Pocket
  BaseFeature = -> Pad002
  Direction = (0,0,1)
  Length = 5
  Length2 = 5
  Profile = -> Sketch005
  ReferenceAxis = -> Sketch005 [N_Axis]
  Refine = true
  Type = 1
FEATURE [Sketcher::SketchObject] Sketch006
  FullyConstrained = true
  MapMode = 5
  Placement = pos=(0,-7.5,0) rot=(1,0,0;1.5708rad)
  Support = -> [Pocket]
  sketch-geometry (1):
    g0: Circle CenterX=6 CenterY=10 CenterZ=0 NormalX=0 NormalY=0 NormalZ=1 AngleXU=0 Radius=1.5
  constraints (3):
    c: DistanceY(g-1,g0) = 10
    c: DistanceX(g-1,g0) = 6
    c: Diameter(g0) = 3
FEATURE [PartDesign::Hole] Hole001
  BaseFeature = -> Pocket
  CustomThreadClearance = 0
  Depth = 25
  DepthType = 0
  Diameter = 4.5
  DrillForDepth = false
  DrillPoint = 1
  DrillPointAngle = 118
  HoleCutCountersinkAngle = 90
  HoleCutCustomValues = false
  HoleCutDepth = 0
  HoleCutDiameter = 6.1
  HoleCutType = 0
  ModelThread = false
  Profile = -> Sketch006
  Refine = true
  Tapered = false
  TaperedAngle = 90
  ThreadClass = 0
  ThreadDepth = 25
  ThreadDepthType = 0
  ThreadDirection = 0
  ThreadFit = 0
  ThreadSize = 11
  ThreadType = 1
  Threaded = false
  UseCustomThreadClearance = false
FEATURE [Sketcher::SketchObject] Sketch007
  ExternalGeometry = -> [Hole001]
  FullyConstrained = true
  MapMode = 5
  Placement = pos=(0,7.5,0) rot=(0,0.707107,0.707107;3.14159rad)
  Support = -> [Hole001]
  sketch-geometry (7):
    g0: LineSegment StartX=-6 StartY=14.0415 StartZ=0 EndX=-9.5 EndY=12.0207 EndZ=0
    g1: LineSegment StartX=-9.5 StartY=12.0207 StartZ=0 EndX=-9.5 EndY=7.97927 EndZ=0
    g2: LineSegment StartX=-9.5 StartY=7.97927 StartZ=0 EndX=-6 EndY=5.95855 EndZ=0
    g3: LineSegment StartX=-6 StartY=5.95855 StartZ=0 EndX=-2.5 EndY=7.97927 EndZ=0
    g4: LineSegment StartX=-2.5 StartY=7.97927 StartZ=0 EndX=-2.5 EndY=12.0207 EndZ=0
    g5: LineSegment StartX=-2.5 StartY=12.0207 StartZ=0 EndX=-6 EndY=14.0415 EndZ=0
    g6: Circle CenterX=-6 CenterY=10 CenterZ=0 NormalX=0 NormalY=0 NormalZ=1 AngleXU=0 Radius=4.04145
  constraints (16):
    c: Coincident(g0,g1)
    c: Coincident(g1,g2)
    c: Coincident(g2,g3)
    c: Coincident(g3,g4)
    c: Coincident(g4,g5)
    c: Coincident(g5,g0)
    c: Equal(g0, g1-g5) x5
    c: PointOnObject(g0,g6)
    c: PointOnObject(g1,g6)
    c: PointOnObject(g2,g6)
    c: PointOnObject(g3,g6)
    c: PointOnObject(g4,g6)
    c: PointOnObject(g5,g6)
    c: Coincident(g6,g-3)
    c: Vertical(g4)
    c: DistanceX(g0,g4) = 7
FEATURE [PartDesign::Pocket] Pocket001
  BaseFeature = -> Hole001
  Direction = (0,-1,2e-16)
  Length = 4
  Length2 = 5
  Profile = -> Sketch007
  ReferenceAxis = -> Sketch007 [N_Axis]
  Refine = true
  Type = 0
FEATURE [Sketcher::SketchObject] Sketch008
  ExternalGeometry = -> [Pocket001]
  FullyConstrained = true
  MapMode = 5
  Placement = pos=(0,0,0) rot=(1,0,0;3.14159rad)
  Support = -> [Pocket001]
  sketch-geometry (5):
    g0: Circle CenterX=-150 CenterY=2.37e-14 CenterZ=0 NormalX=0 NormalY=0 NormalZ=1 AngleXU=0 Radius=8
    g1: ArcOfCircle CenterX=-150 CenterY=2.37e-14 CenterZ=0 NormalX=0 NormalY=0 NormalZ=1 AngleXU=0 Radius=11 StartAngle=0.276227 EndAngle=6.00696
    g2: ArcOfCircle CenterX=0 CenterY=0 CenterZ=0 NormalX=0 NormalY=0 NormalZ=1 AngleXU=0 Radius=7.5 StartAngle=2.73008 EndAngle=3.55311
    g3: LineSegment StartX=-139.417 StartY=3 StartZ=0 EndX=-6.87386 EndY=3 EndZ=0
    g4: LineSegment StartX=-139.417 StartY=-3 StartZ=0 EndX=-6.87386 EndY=-3 EndZ=0
  constraints (14):
    c: Coincident(g1,g0)
    c: Equal(g2,g-3)
    c: Horizontal(g3)
    c: Horizontal(g4)
    c: Coincident(g1,g4)
    c: Coincident(g1,g3)
    c: Coincident(g2,g3)
    c: Coincident(g2,g4)
    c: Symmetric(g1,g1,g-1)
    c: Distance(g1,g1) = 6
    c: Diameter(g0) = 16
    c: Diameter(g1) = 22
    c: DistanceX(g0,g-1) = 150
    c: Coincident(g2,g-3)
FEATURE [PartDesign::Pad] Pad003
  BaseFeature = -> Pocket001
  Direction = (0,0,-1)
  Length = 10
  Length2 = 10
  Profile = -> Sketch008
  ReferenceAxis = -> Sketch008 [N_Axis]
  Refine = true
  Reversed = true
  Type = 0
FEATURE [PartDesign::Plane] DatumPlane
  AttachmentOffset = pos=(0,0,-145) rot=(0,0,1;0rad)
  Length = 60
  MapMode = 5
  Placement = pos=(-130,0,0) rot=(0.57735,0.57735,0.57735;2.0944rad)
  ResizeMode = 0
  Support = -> [Pad003]
  Width = 60
FEATURE [Sketcher::SketchObject] Sketch009
  ExternalGeometry = -> [Pad003]
  FullyConstrained = true
  MapMode = 5
  Placement = pos=(-130,0,0) rot=(0.57735,0.57735,0.57735;2.0944rad)
  Support = -> [DatumPlane]
  sketch-geometry (5):
    g0: Circle CenterX=-1.2e-15 CenterY=32 CenterZ=0 NormalX=0 NormalY=0 NormalZ=1 AngleXU=0 Radius=8
    g1: ArcOfCircle CenterX=-1.2e-15 CenterY=32 CenterZ=0 NormalX=0 NormalY=0 NormalZ=1 AngleXU=0 Radius=11 StartAngle=4.98862 EndAngle=10.7193
    g2: LineSegment StartX=3 StartY=10 StartZ=0 EndX=-3 EndY=10 EndZ=0
    g3: LineSegment StartX=-3 StartY=10 StartZ=0 EndX=-3 EndY=21.417 EndZ=0
    g4: LineSegment StartX=3 StartY=10 StartZ=0 EndX=3 EndY=21.417 EndZ=0
  constraints (12):
    c: Coincident(g0,g-6)
    c: Coincident(g1,g0)
    c: Diameter(g0) = 16
    c: Diameter(g1) = 22
    c: Coincident(g2,g-4)
    c: Coincident(g2,g-5)
    c: Coincident(g2,g3)
    c: Coincident(g2,g4)
    c: Vertical(g4)
    c: Vertical(g3)
    c: Coincident(g1,g3)
    c: Coincident(g1,g4)
FEATURE [PartDesign::Pad] Pad004
  BaseFeature = -> Pad003
  Direction = (1,0,0)
  Length = 5
  Length2 = 10
  Profile = -> Sketch009
  ReferenceAxis = -> Sketch009 [N_Axis]
  Refine = true
  Type = 0
FEATURE [Sketcher::SketchObject] Sketch010
  FullyConstrained = true
  MapMode = 5
  Support = -> [XY_Plane002]
  sketch-geometry (5):
    g0: Circle CenterX=0 CenterY=0 CenterZ=0 NormalX=0 NormalY=0 NormalZ=1 AngleXU=0 Radius=2.5
    g1: ArcOfCircle CenterX=0 CenterY=0 CenterZ=0 NormalX=0 NormalY=0 NormalZ=1 AngleXU=0 Radius=7.5 StartAngle=1.5708 EndAngle=4.71239
    g2: LineSegment StartX=-1.2e-15 StartY=7.5 StartZ=0 EndX=15 EndY=7.5 EndZ=0
    g3: LineSegment StartX=15 StartY=7.5 StartZ=0 EndX=15 EndY=-7.5 EndZ=0
    g4: LineSegment StartX=15 StartY=-7.5 StartZ=0 EndX=1.8e-15 EndY=-7.5 EndZ=0
  constraints (12):
    c: Coincident(g0,g-1)
    c: Coincident(g1,g0)
    c: Diameter(g0) = 5
    c: Diameter(g1) = 15
    c: Horizontal(g2)
    c: Coincident(g2,g3)
    c: Vertical(g3)
    c: Coincident(g3,g4)
    c: Horizontal(g4)
    c: Tangent(g1,g4) = 1.5708
    c: Tangent(g1,g2) = 1.5708
    c: DistanceX(g2,g2) = 15
FEATURE [PartDesign::Pad] Pad005
  Direction = (0,0,1)
  Length = 20
  Length2 = 10
  Profile = -> Sketch010
  ReferenceAxis = -> Sketch010 [N_Axis]
  Refine = true
  Type = 0
FEATURE [Sketcher::SketchObject] Sketch011
  ExternalGeometry = -> [Pad005]
  FullyConstrained = true
  MapMode = 5
  Placement = pos=(15,0,0) rot=(0.57735,0.57735,0.57735;2.0944rad)
  Support = -> [Pad005]
  sketch-geometry (8):
    g0: LineSegment StartX=-7.5 StartY=0 StartZ=0 EndX=-21 EndY=11 EndZ=0
    g1: LineSegment StartX=-21 StartY=11 StartZ=0 EndX=-21 EndY=53 EndZ=0
    g2: LineSegment StartX=-21 StartY=53 StartZ=0 EndX=21 EndY=53 EndZ=0
    g3: LineSegment StartX=21 StartY=53 StartZ=0 EndX=21 EndY=11 EndZ=0
    g4: LineSegment StartX=21 StartY=11 StartZ=0 EndX=7.5 EndY=0 EndZ=0
    g5: LineSegment StartX=7.5 StartY=0 StartZ=0 EndX=-7.5 EndY=0 EndZ=0
    g6: GeomPoint X=-1.2e-15 Y=32 Z=0
    g7: Circle CenterX=-1.2e-15 CenterY=32 CenterZ=0 NormalX=0 NormalY=0 NormalZ=1 AngleXU=0 Radius=11.25
  constraints (18):
    c: PointOnObject(g0,g-1)
    c: Coincident(g0,g1)
    c: Vertical(g1)
    c: Coincident(g1,g2)
    c: Coincident(g2,g3)
    c: Coincident(g3,g4)
    c: Coincident(g4,g5)
    c: Coincident(g5,g0)
    c: Symmetric(g0,g3,g-2)
    c: Symmetric(g1,g2,g-2)
    c: DistanceX(g2,g2) = 42
    c: DistanceY(g3,g3) = 42
    c: Symmetric(g0,g4,g-2)
    c: DistanceX(g5,g5) = 15
    c: Symmetric(g1,g3,g6)
    c: Coincident(g7,g6)
    c: Diameter(g7) = 22.5
    c: DistanceY(g-1,g3) = 11
FEATURE [PartDesign::Pad] Pad006
  BaseFeature = -> Pad005
  Direction = (1,0,0)
  Length = 4
  Length2 = 10
  Profile = -> Sketch011
  ReferenceAxis = -> Sketch011 [N_Axis]
  Refine = true
  Reversed = true
  Type = 0
FEATURE [Sketcher::SketchObject] Sketch012
  ExternalGeometry = -> [Pad006]
  FullyConstrained = true
  MapMode = 5
  Placement = pos=(11,0,0) rot=(0.57735,-0.57735,-0.57735;2.0944rad)
  Support = -> [Pad006]
  sketch-geometry (5):
    g0: Circle CenterX=15.5 CenterY=47.5 CenterZ=0 NormalX=0 NormalY=0 NormalZ=1 AngleXU=0 Radius=1.5
    g1: LineSegment StartX=1.2e-15 StartY=32 StartZ=0 EndX=11.25 EndY=32 EndZ=0
    g2: Circle CenterX=-15.5 CenterY=47.5 CenterZ=0 NormalX=0 NormalY=0 NormalZ=1 AngleXU=0 Radius=1.5
    g3: Circle CenterX=15.5 CenterY=16.5 CenterZ=0 NormalX=0 NormalY=0 NormalZ=1 AngleXU=0 Radius=1.5
    g4: Circle CenterX=-15.5 CenterY=16.5 CenterZ=0 NormalX=0 NormalY=0 NormalZ=1 AngleXU=0 Radius=1.5
  constraints (12):
    c: DistanceY(g-3,g0) = 15.5
    c: DistanceX(g-3,g0) = 15.5
    c: Diameter(g0) = 3
    c: Coincident(g1,g-3)
    c: Horizontal(g1)
    c: PointOnObject(g1,g-3)
    c: Diameter(g2) = 3
    c: Diameter(g3) = 3
    c: Diameter(g4) = 3
    c: Symmetric(g2,g0,g-2)
    c: Symmetric(g4,g3,g-2)
    c: Symmetric(g3,g0,g1)
FEATURE [PartDesign::Hole] Hole002
  BaseFeature = -> Pad006
  CustomThreadClearance = 0
  Depth = 25
  DepthType = 0
  Diameter = 3.4
  DrillForDepth = false
  DrillPoint = 1
  DrillPointAngle = 118
  HoleCutCountersinkAngle = 90
  HoleCutCustomValues = false
  HoleCutDepth = 2
  HoleCutDiameter = 6.1
  HoleCutType = 1
  ModelThread = false
  Profile = -> Sketch012
  Refine = true
  Tapered = false
  TaperedAngle = 90
  ThreadClass = 0
  ThreadDepth = 25
  ThreadDepthType = 0
  ThreadDirection = 0
  ThreadFit = 0
  ThreadSize = 9
  ThreadType = 1
  Threaded = false
  UseCustomThreadClearance = false
FEATURE [Sketcher::SketchObject] Sketch013
  ExternalGeometry = -> [Hole002]
  FullyConstrained = true
  MapMode = 5
  Placement = pos=(0,0,20) rot=(0,0,1;0rad)
  Support = -> [Hole002]
  sketch-geometry (1):
    g0: Circle CenterX=0 CenterY=0 CenterZ=0 NormalX=0 NormalY=0 NormalZ=1 AngleXU=0 Radius=2.5
  constraints (2):
    c: Coincident(g0,g-3)
    c: Equal(g0,g-3)
FEATURE [PartDesign::Pad] Pad007
  BaseFeature = -> Hole002
  Direction = (0,0,1)
  Length = 2
  Length2 = 10
  Profile = -> Sketch013
  ReferenceAxis = -> Sketch013 [N_Axis]
  Refine = true
  Reversed = true
  Type = 0
FEATURE [Sketcher::SketchObject] Sketch017
  ExternalGeometry = -> [Pad007]
  FullyConstrained = true
  MapMode = 5
  Placement = pos=(0,0,0) rot=(1,0,0;3.14159rad)
  sketch-geometry (5):
    g0: Circle CenterX=-150 CenterY=4.1e-15 CenterZ=0 NormalX=0 NormalY=0 NormalZ=1 AngleXU=0 Radius=8
    g1: ArcOfCircle CenterX=-150 CenterY=4.1e-15 CenterZ=0 NormalX=0 NormalY=0 NormalZ=1 AngleXU=0 Radius=11 StartAngle=0.276227 EndAngle=6.00696
    g2: ArcOfCircle CenterX=7.9e-15 CenterY=2e-14 CenterZ=0 NormalX=0 NormalY=0 NormalZ=1 AngleXU=0 Radius=7.5 StartAngle=2.73008 EndAngle=3.55311
    g3: LineSegment StartX=-139.417 StartY=3 StartZ=0 EndX=-6.87386 EndY=3 EndZ=0
    g4: LineSegment StartX=-139.417 StartY=-3 StartZ=0 EndX=-6.87386 EndY=-3 EndZ=0
  constraints (15):
    c: Coincident(g1,g0)
    c: Horizontal(g3)
    c: Horizontal(g4)
    c: Coincident(g1,g4)
    c: Coincident(g1,g3)
    c: Coincident(g2,g3)
    c: Coincident(g2,g4)
    c: Symmetric(g1,g1,g-1)
    c: Distance(g1,g1) = 6
    c: Diameter(g0) = 16
    c: Diameter(g1) = 22
    c: DistanceX(g0,g-1) = 150
    c: Equal(g2,g-3)
    c: PointOnObject(g2,g-3)
    c: Equal(g4,g3)
FEATURE [PartDesign::Pad] Pad008
  BaseFeature = -> Pad007
  Direction = (0,0,-1)
  Length = 10
  Length2 = 10
  Profile = -> Sketch017
  ReferenceAxis = -> Sketch017 [N_Axis]
  Refine = true
  Reversed = true
  Type = 0
FEATURE [PartDesign::Plane] DatumPlane001
  AttachmentOffset = pos=(0,0,-145) rot=(0,0,1;0rad)
  Length = 60
  MapMode = 5
  Placement = pos=(-130,0,0) rot=(0.57735,0.57735,0.57735;2.0944rad)
  ResizeMode = 0
  Support = -> [Pad008]
  Width = 60
FEATURE [Sketcher::SketchObject] Sketch018
  ExternalGeometry = -> [Pad008]
  FullyConstrained = true
  MapMode = 5
  Placement = pos=(-130,0,0) rot=(0.57735,0.57735,0.57735;2.0944rad)
  Support = -> [DatumPlane001]
  sketch-geometry (5):
    g0: Circle CenterX=-1.2e-15 CenterY=32 CenterZ=0 NormalX=0 NormalY=0 NormalZ=1 AngleXU=0 Radius=8
    g1: ArcOfCircle CenterX=-1.2e-15 CenterY=32 CenterZ=0 NormalX=0 NormalY=0 NormalZ=1 AngleXU=0 Radius=11 StartAngle=4.98862 EndAngle=10.7193
    g2: LineSegment StartX=-3 StartY=10 StartZ=0 EndX=-3 EndY=21.417 EndZ=0
    g3: LineSegment StartX=3 StartY=10 StartZ=0 EndX=3 EndY=21.417 EndZ=0
    g4: LineSegment StartX=-3 StartY=10 StartZ=0 EndX=3 EndY=10 EndZ=0
  constraints (12):
    c: Coincident(g0,g-3)
    c: Coincident(g1,g0)
    c: Diameter(g0) = 16
    c: Diameter(g1) = 22
    c: Vertical(g3)
    c: Vertical(g2)
    c: Coincident(g1,g2)
    c: Coincident(g1,g3)
    c: Symmetric(g2,g3,g-2)
    c: Coincident(g4,g2)
    c: Coincident(g4,g3)
    c: Coincident(g2,g-4)
FEATURE [PartDesign::Pad] Pad009
  BaseFeature = -> Pad008
  Direction = (1,0,0)
  Length = 5
  Length2 = 10
  Profile = -> Sketch018
  ReferenceAxis = -> Sketch018 [N_Axis]
  Refine = true
  Type = 0
FEATURE [PartDesign::Body] Body001  label="arm1-skel"
  Group = -> [Sketch010,Pad005,Sketch011,Pad006,Sketch012,Hole002,Sketch013,Pad007,Sketch017,Pad008,DatumPlane001,Sketch018,Pad009]
  Origin = -> Origin002
  Tip = -> Pad009
FEATURE [PartDesign::Chamfer] Chamfer
  Angle = 15
  Base = -> Pad004
  BaseFeature = -> Pad004
  ChamferType = 2
  FlipDirection = true
  Refine = true
  Size = 1
  Size2 = 1
  SupportTransform = false
  UseAllEdges = false
FEATURE [PartDesign::Chamfer] Chamfer001
  Angle = 15
  Base = -> Chamfer [Edge18]
  BaseFeature = -> Chamfer
  ChamferType = 2
  FlipDirection = true
  Refine = true
  Size = 5
  Size2 = 1
  SupportTransform = false
  UseAllEdges = false
FEATURE [PartDesign::Chamfer] Chamfer002
  Angle = 15
  Base = -> Chamfer001 [Edge99]
  BaseFeature = -> Chamfer001
  ChamferType = 2
  FlipDirection = false
  Refine = true
  Size = 1
  Size2 = 1
  SupportTransform = false
  UseAllEdges = false
FEATURE [PartDesign::Chamfer] Chamfer003
  Angle = 15
  Base = -> Chamfer002 [Edge39]
  BaseFeature = -> Chamfer002
  ChamferType = 2
  FlipDirection = true
  Refine = true
  Size = 3
  Size2 = 1
  SupportTransform = false
  UseAllEdges = false
FEATURE [PartDesign::Chamfer] Chamfer004
  Angle = 15
  Base = -> Chamfer003 [Edge79]
  BaseFeature = -> Chamfer003
  ChamferType = 2
  FlipDirection = false
  Refine = true
  Size = 1
  Size2 = 1
  SupportTransform = false
  UseAllEdges = false
FEATURE [PartDesign::Chamfer] Chamfer005
  Angle = 15
  Base = -> Chamfer004 [Edge35,Edge87]
  BaseFeature = -> Chamfer004
  ChamferType = 2
  FlipDirection = true
  Refine = true
  Size = 1
  Size2 = 1
  SupportTransform = false
  UseAllEdges = false
FEATURE [PartDesign::Chamfer] Chamfer006
  Angle = 45
  Base = -> Chamfer005 [Edge5,Edge29]
  BaseFeature = -> Chamfer005
  ChamferType = 0
  FlipDirection = false
  Refine = true
  Size = 7
  Size2 = 1
  SupportTransform = false
  UseAllEdges = false
FEATURE [PartDesign::Plane] DatumPlane002
  Length = 60
  MapMode = 5
  Placement = pos=(-125,0,0) rot=(0.57735,0.57735,0.57735;2.0944rad)
  ResizeMode = 0
  Support = -> [Chamfer006]
  Width = 60
FEATURE [Sketcher::SketchObject] Sketch019
  ExternalGeometry = -> [Chamfer006]
  FullyConstrained = true
  MapMode = 5
  Placement = pos=(-125,0,0) rot=(0.57735,0.57735,0.57735;2.0944rad)
  Support = -> [DatumPlane002]
  sketch-geometry (4):
    g0: ArcOfCircle CenterX=-1.2e-15 CenterY=32 CenterZ=0 NormalX=0 NormalY=0 NormalZ=1 AngleXU=0 Radius=11 StartAngle=3.39743 EndAngle=6.02735
    g1: LineSegment StartX=-10.642 StartY=29.2164 StartZ=0 EndX=-3 EndY=0 EndZ=0
    g2: LineSegment StartX=-3 StartY=0 StartZ=0 EndX=3 EndY=0 EndZ=0
    g3: LineSegment StartX=3 StartY=0 StartZ=0 EndX=10.642 EndY=29.2164 EndZ=0
  constraints (9):
    c: Coincident(g0,g-3)
    c: PointOnObject(g-3,g0)
    c: PointOnObject(g1,g-1)
    c: Coincident(g1,g2)
    c: Coincident(g2,g3)
    c: Tangent(g0,g1) = -1.5708
    c: Tangent(g0,g3) = -1.5708
    c: Distance(g2,g2) = 6
    c: Symmetric(g1,g2,g-2)
FEATURE [PartDesign::Pad] Pad010
  BaseFeature = -> Chamfer006
  Direction = (1,0,0)
  Length = 10
  Length2 = 10
  Profile = -> Sketch019
  ReferenceAxis = -> Sketch019 [N_Axis]
  Refine = true
  Reversed = true
  Type = 3
  UpToFace = -> Chamfer006 [Face1]
FEATURE [PartDesign::Plane] DatumPlane003
  Length = 60
  MapMode = 5
  Placement = pos=(15,0,0) rot=(0.57735,0.57735,0.57735;2.0944rad)
  ResizeMode = 0
  Support = -> [Pad010]
  Width = 60
FEATURE [Sketcher::SketchObject] Sketch020
  ExternalGeometry = -> [Pad010]
  FullyConstrained = true
  MapMode = 5
  Placement = pos=(15,0,0) rot=(0.57735,0.57735,0.57735;2.0944rad)
  Support = -> [DatumPlane003]
  sketch-geometry (4):
    g0: ArcOfCircle CenterX=0 CenterY=47 CenterZ=0 NormalX=0 NormalY=0 NormalZ=1 AngleXU=0 Radius=2 StartAngle=0.664501 EndAngle=2.47709
    g1: ArcOfCircle CenterX=-1.2e-15 CenterY=32 CenterZ=0 NormalX=0 NormalY=0 NormalZ=1 AngleXU=0 Radius=11.25 StartAngle=0.664501 EndAngle=2.47709
    g2: LineSegment StartX=-8.85627 StartY=38.9375 StartZ=0 EndX=-1.57445 EndY=48.2333 EndZ=0
    g3: LineSegment StartX=8.85627 StartY=38.9375 StartZ=0 EndX=1.57445 EndY=48.2333 EndZ=0
  constraints (11):
    c: PointOnObject(g0,g-2)
    c: Coincident(g1,g-3)
    c: PointOnObject(g1,g-3)
    c: Horizontal(g1,g1)
    c: Tangent(g2,g1) = 1.5708
    c: Coincident(g3,g1)
    c: Equal(g3,g2)
    c: Coincident(g0,g2)
    c: Tangent(g0,g3) = -1.5708
    c: DistanceY(g1,g0) = 15
    c: Radius(g0) = 2
FEATURE [PartDesign::Pocket] Pocket002
  BaseFeature = -> Pad010
  Direction = (-1,0,0)
  Length = 5
  Length2 = 5
  Profile = -> Sketch020
  ReferenceAxis = -> Sketch020 [N_Axis]
  Refine = true
  Type = 0
FEATURE [PartDesign::Chamfer] Chamfer007
  Angle = 45
  Base = -> Pocket002 [Edge18,Edge6]
  BaseFeature = -> Pocket002
  ChamferType = 0
  FlipDirection = false
  Refine = true
  Size = 2
  Size2 = 1
  SupportTransform = false
  UseAllEdges = false
FEATURE [PartDesign::Fillet] Fillet
  Base = -> Chamfer007 [Edge65,Edge142,Edge84,Edge143]
  BaseFeature = -> Chamfer007
  Radius = 6
  Refine = true
  SupportTransform = false
  UseAllEdges = false
FEATURE [PartDesign::Body] Body  label="arm1s"
  Group = -> [Sketch,Pad,Sketch001,Pad001,Sketch003,Hole,Sketch004,Pad002,Sketch005,Pocket,Sketch006,Hole001,Sketch007,Pocket001,Sketch008,Pad003,DatumPlane,Sketch009,Pad004,Chamfer,Chamfer001,Chamfer002,Chamfer003,Chamfer004,Chamfer005,Chamfer006,DatumPlane002,Sketch019,Pad010,DatumPlane003,Sketch020,Pocket002,Chamfer007,Fillet]
  Origin = -> Origin001
  Tip = -> Fillet
FEATURE [App::Part] Part  label="arm1"
  Group = -> [Body001,Body]
  Origin = -> Origin
---- part arm2.FCStd = doc fcstd_e9f4b0e10bbd ----
FCSTD DOCUMENT  (FreeCAD 2024.1R35694 (Git))
Label: arm2
License: All rights reserved
LicenseURL: https://en.wikipedia.org/wiki/All_rights_reserved
objects: Sketcher::SketchObject×3, PartDesign::Pad×2, PartDesign::Body×2, PartDesign::Chamfer×1, PartDesign::Pocket×1, App::Part×1
note: 13 computed .brp shape members not serialized (recipe doc carries the construction recipe); baked Part::Feature solids carry a one-line shape summary decoded from their .brp

FEATURE [Sketcher::SketchObject] Sketch
  FullyConstrained = true
  MapMode = 5
  Support = -> [XY_Plane001]
  sketch-geometry (9):
    g0: ArcOfCircle CenterX=0 CenterY=0 CenterZ=0 NormalX=0 NormalY=0 NormalZ=1 AngleXU=0 Radius=2.5 StartAngle=2.2143 EndAngle=4.06889
    g1: ArcOfCircle CenterX=0 CenterY=0 CenterZ=0 NormalX=0 NormalY=0 NormalZ=1 AngleXU=0 Radius=4 StartAngle=0.523599 EndAngle=5.75959
    g2: LineSegment StartX=3.4641 StartY=2 StartZ=0 EndX=118 EndY=2 EndZ=0
    g3: LineSegment StartX=118 StartY=2 StartZ=0 EndX=120 EndY=0 EndZ=0
    g4: LineSegment StartX=120 StartY=0 StartZ=0 EndX=118 EndY=-2 EndZ=0
    g5: LineSegment StartX=118 StartY=-2 StartZ=0 EndX=3.4641 EndY=-2 EndZ=0
    g6: LineSegment StartX=-1.5 StartY=2 StartZ=0 EndX=1.5 EndY=2 EndZ=0
    g7: LineSegment StartX=-1.5 StartY=-2 StartZ=0 EndX=1.5 EndY=-2 EndZ=0
    g8: ArcOfCircle CenterX=0 CenterY=0 CenterZ=0 NormalX=0 NormalY=0 NormalZ=1 AngleXU=0 Radius=2.5 StartAngle=5.35589 EndAngle=7.21048
  constraints (26):
    c: Coincident(g0,g-1)
    c: Coincident(g1,g0)
    c: Horizontal(g2)
    c: Coincident(g2,g3)
    c: PointOnObject(g3,g-1)
    c: Coincident(g3,g4)
    c: Coincident(g4,g5)
    c: Horizontal(g6)
    c: Horizontal(g7)
    c: Equal(g6,g7)
    c: Coincident(g0,g6)
    c: Equal(g0,g8)
    c: Coincident(g0,g7)
    c: Coincident(g8,g7)
    c: Coincident(g0,g8)
    c: Diameter(g8) = 5
    c: DistanceY(g7,g6) = 4
    c: Symmetric(g4,g2,g-1)
    c: Angle(g3,g4) = 1.5708
    c: Distance(g2,g4) = 4
    c: Coincident(g1,g5)
    c: Diameter(g1) = 8
    c: DistanceX(g-1,g3) = 120
    c: Coincident(g1,g2)
    c: Equal(g5,g2)
    c: Coincident(g6,g8)
FEATURE [PartDesign::Pad] Pad
  Direction = (0,0,1)
  Length = 5
  Length2 = 10
  Profile = -> Sketch
  ReferenceAxis = -> Sketch [N_Axis]
  Refine = true
  Type = 0
FEATURE [PartDesign::Body] Body  label="arm2-skel"
  Group = -> [Sketch,Pad]
  Origin = -> Origin001
  Tip = -> Pad
FEATURE [Sketcher::SketchObject] Sketch001
  FullyConstrained = true
  MapMode = 5
  Support = -> [XY_Plane002]
  sketch-geometry (9):
    g0: ArcOfCircle CenterX=0 CenterY=0 CenterZ=0 NormalX=0 NormalY=0 NormalZ=1 AngleXU=0 Radius=2.5 StartAngle=2.2143 EndAngle=4.06889
    g1: ArcOfCircle CenterX=0 CenterY=0 CenterZ=0 NormalX=0 NormalY=0 NormalZ=1 AngleXU=0 Radius=4 StartAngle=0.523599 EndAngle=5.75959
    g2: LineSegment StartX=3.4641 StartY=2 StartZ=0 EndX=118 EndY=2 EndZ=0
    g3: LineSegment StartX=118 StartY=2 StartZ=0 EndX=120 EndY=0 EndZ=0
    g4: LineSegment StartX=120 StartY=0 StartZ=0 EndX=118 EndY=-2 EndZ=0
    g5: LineSegment StartX=118 StartY=-2 StartZ=0 EndX=3.4641 EndY=-2 EndZ=0
    g6: LineSegment StartX=-1.5 StartY=2 StartZ=0 EndX=1.5 EndY=2 EndZ=0
    g7: LineSegment StartX=-1.5 StartY=-2 StartZ=0 EndX=1.5 EndY=-2 EndZ=0
    g8: ArcOfCircle CenterX=0 CenterY=0 CenterZ=0 NormalX=0 NormalY=0 NormalZ=1 AngleXU=0 Radius=2.5 StartAngle=5.35589 EndAngle=7.21048
  constraints (26):
    c: Coincident(g0,g-1)
    c: Coincident(g1,g0)
    c: Horizontal(g2)
    c: Coincident(g2,g3)
    c: PointOnObject(g3,g-1)
    c: Coincident(g3,g4)
    c: Coincident(g4,g5)
    c: Horizontal(g6)
    c: Horizontal(g7)
    c: Equal(g6,g7)
    c: Coincident(g0,g6)
    c: Equal(g0,g8)
    c: Coincident(g0,g7)
    c: Coincident(g8,g7)
    c: Coincident(g0,g8)
    c: Diameter(g8) = 5
    c: DistanceY(g7,g6) = 4
    c: Symmetric(g4,g2,g-1)
    c: Angle(g3,g4) = 1.5708
    c: Distance(g2,g4) = 4
    c: Coincident(g1,g5)
    c: Diameter(g1) = 8
    c: DistanceX(g-1,g3) = 120
    c: Coincident(g1,g2)
    c: Equal(g5,g2)
    c: Coincident(g6,g8)
FEATURE [PartDesign::Pad] Pad001
  Direction = (0,0,1)
  Length = 5
  Length2 = 10
  Profile = -> Sketch001
  ReferenceAxis = -> Sketch001 [N_Axis]
  Refine = true
  Type = 0
FEATURE [PartDesign::Chamfer] Chamfer
  Angle = 15
  Base = -> Pad001 [Edge24,Edge21,Edge18,Edge26,Edge25,Edge27,Edge19,Edge22]
  BaseFeature = -> Pad001
  ChamferType = 2
  FlipDirection = false
  Refine = true
  Size = 1
  Size2 = 1
  SupportTransform = false
  UseAllEdges = false
FEATURE [Sketcher::SketchObject] Sketch002
  ExternalGeometry = -> [Chamfer]
  FullyConstrained = true
  MapMode = 5
  Placement = pos=(0,0,5) rot=(0,0,1;0rad)
  Support = -> [Chamfer]
  sketch-geometry (4):
    g0: LineSegment StartX=3.4641 StartY=-2 StartZ=0 EndX=203.464 EndY=-2 EndZ=0
    g1: LineSegment StartX=203.464 StartY=-2 StartZ=0 EndX=203.464 EndY=2 EndZ=0
    g2: LineSegment StartX=203.464 StartY=2 StartZ=0 EndX=3.4641 EndY=2 EndZ=0
    g3: ArcOfCircle CenterX=0 CenterY=0 CenterZ=0 NormalX=0 NormalY=0 NormalZ=1 AngleXU=0 Radius=4 StartAngle=5.75959 EndAngle=6.80678
  constraints (11):
    c: Coincident(g0,g1)
    c: Coincident(g1,g2)
    c: Vertical(g1)
    c: Horizontal(g0)
    c: Horizontal(g2)
    c: Coincident(g3,g-3)
    c: Coincident(g2,g-3)
    c: Coincident(g0,g-3)
    c: DistanceX(g2,g2) = 200
    c: Coincident(g3,g2)
    c: PointOnObject(g3,g0)
FEATURE [PartDesign::Pocket] Pocket
  BaseFeature = -> Chamfer
  Direction = (0,0,-1)
  Length = 1
  Length2 = 5
  Profile = -> Sketch002
  ReferenceAxis = -> Sketch002 [N_Axis]
  Refine = true
  Type = 0
FEATURE [PartDesign::Body] Body001  label="arm2s"
  Group = -> [Sketch001,Pad001,Chamfer,Sketch002,Pocket]
  Origin = -> Origin002
  Tip = -> Pocket
FEATURE [App::Part] Part  label="arm2"
  Group = -> [Body,Body001]
  Origin = -> Origin
---- part base.FCStd = doc fcstd_e9e477c1d145 ----
FCSTD DOCUMENT  (FreeCAD 2024.1R35694 (Git))
Label: base
License: All rights reserved
LicenseURL: https://en.wikipedia.org/wiki/All_rights_reserved
objects: Sketcher::SketchObject×6, PartDesign::Pocket×2, PartDesign::Pad×1, PartDesign::Plane×1, PartDesign::AdditiveLoft×1, PartDesign::Hole×1, PartDesign::PolarPattern×1, PartDesign::Body×1, App::Part×1
note: 19 computed .brp shape members not serialized (recipe doc carries the construction recipe); baked Part::Feature solids carry a one-line shape summary decoded from their .brp

FEATURE [Sketcher::SketchObject] Sketch
  FullyConstrained = true
  MapMode = 5
  Support = -> [XY_Plane001]
  sketch-geometry (4):
    g0: LineSegment StartX=-25 StartY=-25 StartZ=0 EndX=25 EndY=-25 EndZ=0
    g1: LineSegment StartX=25 StartY=-25 StartZ=0 EndX=25 EndY=25 EndZ=0
    g2: LineSegment StartX=25 StartY=25 StartZ=0 EndX=-25 EndY=25 EndZ=0
    g3: LineSegment StartX=-25 StartY=25 StartZ=0 EndX=-25 EndY=-25 EndZ=0
  constraints (11):
    c: Coincident(g0,g1)
    c: Coincident(g1,g2)
    c: Coincident(g2,g3)
    c: Coincident(g3,g0)
    c: Horizontal(g0)
    c: Horizontal(g2)
    c: Vertical(g1)
    c: Vertical(g3)
    c: Symmetric(g0,g1,g-1)
    c: Equal(g1,g2)
    c: DistanceY(g1,g1) = 50
FEATURE [PartDesign::Pad] Pad
  Direction = (0,0,1)
  Length = 4
  Length2 = 10
  Profile = -> Sketch
  ReferenceAxis = -> Sketch [N_Axis]
  Refine = true
  Type = 0
FEATURE [PartDesign::Plane] DatumPlane
  AttachmentOffset = pos=(0,0,-50) rot=(0,0,1;0rad)
  Length = 120
  MapMode = 5
  Placement = pos=(0,0,-50) rot=(0,0,1;0rad)
  ResizeMode = 0
  Support = -> [XY_Plane001]
  Width = 120
FEATURE [Sketcher::SketchObject] Sketch001
  ExternalGeometry = -> [Pad]
  FullyConstrained = true
  MapMode = 5
  Support = -> [XY_Plane001]
  sketch-geometry (10):
    g0: LineSegment StartX=-25 StartY=25 StartZ=0 EndX=-25 EndY=-25 EndZ=0
    g1: LineSegment StartX=-25 StartY=-25 StartZ=0 EndX=25 EndY=-25 EndZ=0
    g2: LineSegment StartX=25 StartY=-25 StartZ=0 EndX=25 EndY=25 EndZ=0
    g3: LineSegment StartX=25 StartY=25 StartZ=0 EndX=-25 EndY=25 EndZ=0
    g4: GeomPoint X=0 Y=0 Z=0
    g5: LineSegment StartX=-23 StartY=23 StartZ=0 EndX=-23 EndY=-23 EndZ=0
    g6: LineSegment StartX=-23 StartY=-23 StartZ=0 EndX=23 EndY=-23 EndZ=0
    g7: LineSegment StartX=23 StartY=-23 StartZ=0 EndX=23 EndY=23 EndZ=0
    g8: LineSegment StartX=23 StartY=23 StartZ=0 EndX=-23 EndY=23 EndZ=0
    g9: GeomPoint X=0 Y=0 Z=0
  constraints (23):
    c: Coincident(g0,g1)
    c: Coincident(g1,g2)
    c: Coincident(g2,g3)
    c: Coincident(g3,g0)
    c: Vertical(g0)
    c: Vertical(g2)
    c: Horizontal(g1)
    c: Horizontal(g3)
    c: Symmetric(g2,g0,g4)
    c: Coincident(g4,g-1)
    c: Coincident(g1,g-4)
    c: Coincident(g5,g6)
    c: Coincident(g6,g7)
    c: Coincident(g7,g8)
    c: Coincident(g8,g5)
    c: Vertical(g5)
    c: Vertical(g7)
    c: Horizontal(g6)
    c: Horizontal(g8)
    c: Symmetric(g7,g5,g9)
    c: Coincident(g9,g4)
    c: DistanceX(g7,g2) = 2
    c: DistanceY(g7,g2) = 2
FEATURE [Sketcher::SketchObject] Sketch002
  FullyConstrained = true
  MapMode = 5
  Placement = pos=(0,0,-50) rot=(0,0,1;0rad)
  Support = -> [DatumPlane]
  sketch-geometry (10):
    g0: LineSegment StartX=-50 StartY=-50 StartZ=0 EndX=50 EndY=-50 EndZ=0
    g1: LineSegment StartX=50 StartY=-50 StartZ=0 EndX=50 EndY=50 EndZ=0
    g2: LineSegment StartX=50 StartY=50 StartZ=0 EndX=-50 EndY=50 EndZ=0
    g3: LineSegment StartX=-50 StartY=50 StartZ=0 EndX=-50 EndY=-50 EndZ=0
    g4: GeomPoint X=0 Y=0 Z=0
    g5: LineSegment StartX=-48 StartY=-48 StartZ=0 EndX=48 EndY=-48 EndZ=0
    g6: LineSegment StartX=48 StartY=-48 StartZ=0 EndX=48 EndY=48 EndZ=0
    g7: LineSegment StartX=48 StartY=48 StartZ=0 EndX=-48 EndY=48 EndZ=0
    g8: LineSegment StartX=-48 StartY=48 StartZ=0 EndX=-48 EndY=-48 EndZ=0
    g9: GeomPoint X=0 Y=0 Z=0
  constraints (24):
    c: Coincident(g0,g1)
    c: Coincident(g1,g2)
    c: Coincident(g2,g3)
    c: Coincident(g3,g0)
    c: Horizontal(g0)
    c: Horizontal(g2)
    c: Vertical(g1)
    c: Vertical(g3)
    c: Symmetric(g2,g0,g4)
    c: Coincident(g4,g-1)
    c: Coincident(g5,g6)
    c: Coincident(g6,g7)
    c: Coincident(g7,g8)
    c: Coincident(g8,g5)
    c: Horizontal(g5)
    c: Horizontal(g7)
    c: Vertical(g6)
    c: Vertical(g8)
    c: Symmetric(g7,g5,g9)
    c: Coincident(g9,g4)
    c: Equal(g7,g6)
    c: Equal(g1,g2)
    c: DistanceX(g6,g1) = 2
    c: DistanceY(g1,g1) = 100
FEATURE [PartDesign::AdditiveLoft] AdditiveLoft
  BaseFeature = -> Pad
  Closed = false
  Profile = -> Sketch001
  Refine = true
  Ruled = false
  Sections = -> [Sketch002]
FEATURE [Sketcher::SketchObject] Sketch003
  FullyConstrained = true
  MapMode = 5
  Placement = pos=(0,0,4) rot=(0,0,1;0rad)
  sketch-geometry (1):
    g0: Circle CenterX=0 CenterY=0 CenterZ=0 NormalX=0 NormalY=0 NormalZ=1 AngleXU=0 Radius=11.25
  constraints (2):
    c: Coincident(g0,g-1)
    c: Diameter(g0) = 22.5
FEATURE [PartDesign::Pocket] Pocket
  BaseFeature = -> AdditiveLoft
  Direction = (0,0,-1)
  Length = 5
  Length2 = 5
  Profile = -> Sketch003
  ReferenceAxis = -> Sketch003 [N_Axis]
  Refine = true
  Type = 0
FEATURE [Sketcher::SketchObject] Sketch004
  FullyConstrained = true
  MapMode = 5
  Placement = pos=(0,0,4) rot=(0,0,1;0rad)
  Support = -> [Pocket]
  sketch-geometry (4):
    g0: Circle CenterX=15.5 CenterY=15.5 CenterZ=0 NormalX=0 NormalY=0 NormalZ=1 AngleXU=0 Radius=1.5
    g1: Circle CenterX=15.5 CenterY=-15.5 CenterZ=0 NormalX=0 NormalY=0 NormalZ=1 AngleXU=0 Radius=1.5
    g2: Circle CenterX=-15.5 CenterY=-15.5 CenterZ=0 NormalX=0 NormalY=0 NormalZ=1 AngleXU=0 Radius=1.5
    g3: Circle CenterX=-15.5 CenterY=15.5 CenterZ=0 NormalX=0 NormalY=0 NormalZ=1 AngleXU=0 Radius=1.5
  constraints (9):
    c: Symmetric(g3,g0,g-2)
    c: Symmetric(g2,g3,g-1)
    c: Symmetric(g2,g1,g-2)
    c: Equal(g0,g3)
    c: Equal(g2,g1)
    c: Equal(g2,g3)
    c: Diameter(g3) = 3
    c: DistanceX(g3,g0) = 31
    c: DistanceY(g2,g3) = 31
FEATURE [PartDesign::Hole] Hole
  BaseFeature = -> Pocket
  CustomThreadClearance = 0
  Depth = 253.234
  DepthType = 1
  Diameter = 3.4
  DrillForDepth = false
  DrillPoint = 1
  DrillPointAngle = 118
  HoleCutCountersinkAngle = 90
  HoleCutCustomValues = false
  HoleCutDepth = 2
  HoleCutDiameter = 6.1
  HoleCutType = 1
  ModelThread = false
  Profile = -> Sketch004
  Refine = true
  Tapered = false
  TaperedAngle = 90
  ThreadClass = 0
  ThreadDepth = 253.234
  ThreadDepthType = 0
  ThreadDirection = 0
  ThreadFit = 0
  ThreadSize = 9
  ThreadType = 1
  Threaded = false
  UseCustomThreadClearance = false
FEATURE [Sketcher::SketchObject] Sketch005
  ExternalGeometry = -> [Hole]
  FullyConstrained = true
  MapMode = 5
  Placement = pos=(0,0,0) rot=(1,0,0;1.5708rad)
  Support = -> [XZ_Plane001]
  sketch-geometry (6):
    g0: ArcOfCircle CenterX=0 CenterY=-40 CenterZ=0 NormalX=0 NormalY=0 NormalZ=1 AngleXU=0 Radius=5 StartAngle=3.54648 EndAngle=5.87829
    g1: ArcOfCircle CenterX=-15 CenterY=-5 CenterZ=0 NormalX=0 NormalY=0 NormalZ=1 AngleXU=0 Radius=5 StartAngle=1.5708 EndAngle=3.54648
    g2: ArcOfCircle CenterX=15 CenterY=-5 CenterZ=0 NormalX=0 NormalY=0 NormalZ=1 AngleXU=0 Radius=5 StartAngle=5.87829 EndAngle=7.85398
    g3: LineSegment StartX=-15 StartY=-5.77e-14 StartZ=0 EndX=15 EndY=-5.77e-14 EndZ=0
    g4: LineSegment StartX=19.5957 StartY=-6.9696 StartZ=0 EndX=4.59573 EndY=-41.9696 EndZ=0
    g5: LineSegment StartX=-4.59573 StartY=-41.9696 StartZ=0 EndX=-19.5957 EndY=-6.9696 EndZ=0
  constraints (14):
    c: PointOnObject(g0,g-2)
    c: Tangent(g1,g-3)
    c: Horizontal(g3)
    c: Tangent(g0,g4) = 1.5708
    c: Tangent(g0,g5) = 1.5708
    c: Tangent(g2,g4) = 1.5708
    c: Tangent(g1,g5) = 1.5708
    c: Tangent(g2,g3) = 1.5708
    c: Equal(g0,g2)
    c: Radius(g0) = 5
    c: DistanceY(g0,g-1) = 40
    c: DistanceX(g1,g2) = 30
    c: Tangent(g1,g3) = 1.5708
    c: Symmetric(g1,g2,g-2)
FEATURE [PartDesign::Pocket] Pocket001
  BaseFeature = -> Hole
  Direction = (0,1,-2e-16)
  Length = 5
  Length2 = 5
  Profile = -> Sketch005
  ReferenceAxis = -> Sketch005 [N_Axis]
  Refine = true
  Type = 1
FEATURE [PartDesign::PolarPattern] PolarPattern
  Angle = 360
  Axis = -> Z_Axis001
  BaseFeature = -> Pocket001
  Mode = 0
  Occurrences = 4
  Offset = 120
  Originals = -> [Pocket001]
  Refine = true
FEATURE [PartDesign::Body] Body  label="base-skel"
  Group = -> [Sketch,Pad,DatumPlane,Sketch001,Sketch002,AdditiveLoft,Sketch003,Pocket,Sketch004,Hole,Sketch005,Pocket001,PolarPattern]
  Origin = -> Origin001
  Tip = -> PolarPattern
FEATURE [App::Part] Part  label="base"
  Group = -> [Body]
  Origin = -> Origin
---- part bearing625.FCStd = doc fcstd_0c16b8e61179 ----
FCSTD DOCUMENT  (FreeCAD 2024.1R35694 (Git))
Label: bearing625
License: All rights reserved
LicenseURL: http://en.wikipedia.org/wiki/All_rights_reserved
objects: Sketcher::SketchObject×1, PartDesign::Pad×1, PartDesign::Body×1, App::Part×1
note: 4 computed .brp shape members not serialized (recipe doc carries the construction recipe); baked Part::Feature solids carry a one-line shape summary decoded from their .brp

FEATURE [Sketcher::SketchObject] Sketch
  FullyConstrained = false
  MapMode = 5
  Support = -> [XY_Plane]
  sketch-geometry (2):
    g0: Circle CenterX=0 CenterY=0 CenterZ=0 NormalX=0 NormalY=0 NormalZ=1 AngleXU=0 Radius=2.5
    g1: Circle CenterX=0 CenterY=0 CenterZ=0 NormalX=0 NormalY=0 NormalZ=1 AngleXU=0 Radius=8
  constraints (4):
    c: Coincident(g0,g-1)
    c: Coincident(g1,g0)
    c: Diameter(g0) = 5
    c: Diameter(g1) = 16
FEATURE [PartDesign::Pad] Pad
  Direction = (1,1,1)
  Length = 5
  Length2 = 100
  Profile = -> Sketch
  Type = 0
FEATURE [PartDesign::Body] Body  label="bearing625"
  Group = -> [Sketch,Pad]
  Origin = -> Origin
  Placement = pos=(0,0,0) rot=(0,-1,0;4.71239rad)
  Tip = -> Pad
FEATURE [App::Part] Part  label="b625"
  Group = -> [Body]
  Origin = -> Origin001
---- part bevel_gear.FCStd = doc fcstd_19eadd010346 ----
FCSTD DOCUMENT  (FreeCAD 0.22R35966 (Git))
Label: bevel_gear
License: All rights reserved
LicenseURL: https://en.wikipedia.org/wiki/All_rights_reserved
objects: Sketcher::SketchObject×3, Part::FeaturePython×1, PartDesign::FeatureBase×1, PartDesign::Pocket×1, PartDesign::Groove×1, PartDesign::Chamfer×1, PartDesign::CoordinateSystem×1, PartDesign::Body×1, App::Part×1
note: 13 computed .brp shape members not serialized (recipe doc carries the construction recipe); baked Part::Feature solids carry a one-line shape summary decoded from their .brp

FEATURE [Part::FeaturePython] BevelGear  # WARN: FeaturePython — macro-defined, semantics opaque (R4)
  AttacherType = Attacher::AttachEngine3D
  angular_backlash = 0
  backlash = 0
  beta = 0
  clearance = 0.1
  dw = 36
  height = 7
  module = 2
  numpoints = 20
  pitch_angle = 45
  pressure_angle = 20
  reset_origin = true
  teeth = 18
  version = 1.2.0
  expr: angular_backlash = backlash / dw * 360 ° / pi
  expr: dw = teeth * module
FEATURE [PartDesign::FeatureBase] BaseFeature
  BaseFeature = -> BevelGear
  Suppressed = false
FEATURE [Sketcher::SketchObject] Sketch001
  FullyConstrained = true
  MapMode = 5
  Support = -> [XY_Plane001]
  sketch-geometry (4):
    g0: ArcOfCircle CenterX=0 CenterY=0 CenterZ=0 NormalX=0 NormalY=0 NormalZ=1 AngleXU=0 Radius=2.5 StartAngle=5.35589 EndAngle=7.21048
    g1: LineSegment StartX=-1.5 StartY=2 StartZ=0 EndX=1.5 EndY=2 EndZ=0
    g2: LineSegment StartX=-1.5 StartY=-2 StartZ=0 EndX=1.5 EndY=-2 EndZ=0
    g3: ArcOfCircle CenterX=0 CenterY=0 CenterZ=0 NormalX=0 NormalY=0 NormalZ=1 AngleXU=0 Radius=2.5 StartAngle=2.2143 EndAngle=4.06889
  constraints (12):
    c: Coincident(g0,g-1)
    c: Horizontal(g1)
    c: Horizontal(g2)
    c: Equal(g1,g2)
    c: Coincident(g3,g2)
    c: Coincident(g0,g2)
    c: Equal(g0,g3)
    c: Coincident(g0,g1)
    c: Coincident(g3,g1)
    c: Coincident(g0,g3)
    c: Diameter(g0) = 5
    c: Distance(g0,g2) = 4
FEATURE [PartDesign::Pocket] Pocket
  BaseFeature = -> BaseFeature
  Direction = (0,0,-1)
  Length = 5
  Length2 = 5
  Midplane = true
  Profile = -> Sketch001
  ReferenceAxis = -> Sketch001 [N_Axis]
  Refine = true
  Suppressed = false
  Type = 1
FEATURE [Sketcher::SketchObject] Sketch
  FullyConstrained = true
  MapMode = 5
  Placement = pos=(0,0,0) rot=(0.57735,0.57735,0.57735;2.0944rad)
  Support = -> [YZ_Plane001]
  sketch-geometry (3):
    g0: LineSegment StartX=-18 StartY=0 StartZ=0 EndX=0 EndY=18 EndZ=0
    g1: LineSegment StartX=0 StartY=18 StartZ=0 EndX=18 EndY=0 EndZ=0
    g2: LineSegment StartX=18 StartY=0 StartZ=0 EndX=-18 EndY=0 EndZ=0
  constraints (9):
    c: PointOnObject(g0,g-1)
    c: PointOnObject(g0,g-2)
    c: Coincident(g0,g1)
    c: PointOnObject(g1,g-1)
    c: Coincident(g1,g2)
    c: Coincident(g2,g0)
    c: Equal(g0,g1)
    c: DistanceX(g2,g2) = 36
    c: Angle(g0,g1) = 1.5708
FEATURE [Sketcher::SketchObject] Sketch002
  FullyConstrained = true
  MapMode = 5
  Placement = pos=(0,0,0) rot=(0.57735,0.57735,0.57735;2.0944rad)
  Support = -> [YZ_Plane001]
  sketch-geometry (3):
    g0: LineSegment StartX=13 StartY=0 StartZ=0 EndX=23 EndY=10 EndZ=0
    g1: LineSegment StartX=23 StartY=10 StartZ=0 EndX=23 EndY=0 EndZ=0
    g2: LineSegment StartX=23 StartY=0 StartZ=0 EndX=13 EndY=0 EndZ=0
  constraints (9):
    c: PointOnObject(g0,g-1)
    c: Coincident(g0,g1)
    c: PointOnObject(g1,g-1)
    c: Coincident(g1,g2)
    c: Coincident(g2,g0)
    c: DistanceX(g-1,g0) = 13
    c: DistanceX(g2,g2) = 10
    c: Vertical(g1)
    c: Angle(g2,g0) = 0.785398
FEATURE [PartDesign::Groove] Groove
  Angle = 360
  Angle2 = 60
  Axis = (0,0,1)
  Base = (0,0,0)
  BaseFeature = -> Pocket
  Profile = -> Sketch002
  ReferenceAxis = -> Sketch002 [V_Axis]
  Refine = true
  Suppressed = false
  Type = 0
FEATURE [PartDesign::Chamfer] Chamfer
  Angle = 15
  Base = -> Groove [Edge339,Edge337,Edge334,Edge335,Edge336,Edge338]
  BaseFeature = -> Groove
  ChamferType = 2
  FlipDirection = true
  Refine = true
  Size = 1
  Size2 = 1
  SupportTransform = false
  Suppressed = false
  UseAllEdges = false
FEATURE [PartDesign::CoordinateSystem] Local_CS
  AttacherType = Attacher::AttachEngine3D
  MapMode = 45
  Placement = pos=(5.50499e-08,-6.7455e-08,0) rot=(0,0,-1;1.2e-05rad)
  Support = -> [Chamfer]
FEATURE [PartDesign::Body] Body  label="gear"
  BaseFeature = -> BevelGear
  Group = -> [BaseFeature,Sketch001,Pocket,Sketch,Sketch002,Groove,Chamfer,Local_CS]
  Origin = -> Origin001
  Tip = -> Chamfer
FEATURE [App::Part] Part  label="bevel_gear"
  Group = -> [Body,BevelGear]
  Origin = -> Origin
---- part nema17-48.FCStd = doc fcstd_ca372efca2bd ----
FCSTD DOCUMENT  (FreeCAD 2024.1R35694 (Git))
Label: nema17-48
License: All rights reserved
LicenseURL: http://en.wikipedia.org/wiki/All_rights_reserved
objects: Sketcher::SketchObject×4, PartDesign::Pad×3, PartDesign::Chamfer×2, PartDesign::Hole×1, PartDesign::Body×1, App::Part×1
note: 17 computed .brp shape members not serialized (recipe doc carries the construction recipe); baked Part::Feature solids carry a one-line shape summary decoded from their .brp

FEATURE [Sketcher::SketchObject] Sketch
  FullyConstrained = false
  MapMode = 5
  Support = -> [XY_Plane]
  sketch-geometry (5):
    g0: LineSegment StartX=21.15 StartY=21.15 StartZ=0 EndX=-21.15 EndY=21.15 EndZ=0
    g1: LineSegment StartX=-21.15 StartY=21.15 StartZ=0 EndX=-21.15 EndY=-21.15 EndZ=0
    g2: LineSegment StartX=-21.15 StartY=-21.15 StartZ=0 EndX=21.15 EndY=-21.15 EndZ=0
    g3: LineSegment StartX=21.15 StartY=-21.15 StartZ=0 EndX=21.15 EndY=21.15 EndZ=0
    g4: Circle CenterX=0 CenterY=0 CenterZ=0 NormalX=0 NormalY=0 NormalZ=1 AngleXU=0 Radius=29.9106
  constraints (14):
    c: Coincident(g0,g1)
    c: Coincident(g1,g2)
    c: Coincident(g2,g3)
    c: Coincident(g3,g0)
    c: Equal(g0,g1)
    c: Equal(g0,g2)
    c: Equal(g0,g3)
    c: PointOnObject(g0,g4)
    c: PointOnObject(g1,g4)
    c: PointOnObject(g2,g4)
    c: PointOnObject(g3,g4)
    c: Coincident(g4,g-1)
    c: Horizontal(g0)
    c: DistanceY(g3,g3) = 42.3
FEATURE [PartDesign::Pad] Pad
  Direction = (0,0,1)
  Length = 48
  Length2 = 100
  Profile = -> Sketch
  ReferenceAxis = -> Sketch [N_Axis]
  Type = 0
FEATURE [Sketcher::SketchObject] Sketch001
  FullyConstrained = true
  MapMode = 5
  Placement = pos=(0,0,48) rot=(0,0,1;0rad)
  Support = -> [Pad]
  sketch-geometry (1):
    g0: Circle CenterX=0 CenterY=0 CenterZ=0 NormalX=0 NormalY=0 NormalZ=1 AngleXU=0 Radius=11
  constraints (2):
    c: Coincident(g0,g-1)
    c: Diameter(g0) = 22
FEATURE [PartDesign::Pad] Pad001
  BaseFeature = -> Pad
  Direction = (0,0,1)
  Length = 2
  Length2 = 100
  Profile = -> Sketch001
  ReferenceAxis = -> Sketch001 [N_Axis]
  Type = 0
FEATURE [Sketcher::SketchObject] Sketch002
  FullyConstrained = true
  MapMode = 5
  Placement = pos=(0,0,48) rot=(0,0,1;0rad)
  Support = -> [Pad001]
  sketch-geometry (1):
    g0: Circle CenterX=0 CenterY=0 CenterZ=0 NormalX=0 NormalY=0 NormalZ=1 AngleXU=0 Radius=2.5
  constraints (2):
    c: Coincident(g0,g-1)
    c: Diameter(g0) = 5
FEATURE [PartDesign::Pad] Pad002
  BaseFeature = -> Pad001
  Direction = (0,0,1)
  Length = 24
  Length2 = 100
  Profile = -> Sketch002
  ReferenceAxis = -> Sketch002 [N_Axis]
  Type = 0
FEATURE [PartDesign::Chamfer] Chamfer
  Angle = 45
  Base = -> Pad002 [Edge18]
  BaseFeature = -> Pad002
  ChamferType = 0
  FlipDirection = false
  Size = 0.5
  Size2 = 1
  SupportTransform = true
  UseAllEdges = false
FEATURE [Sketcher::SketchObject] Sketch004
  FullyConstrained = true
  MapMode = 5
  Placement = pos=(0,0,48) rot=(0,0,1;0rad)
  sketch-geometry (4):
    g0: Circle CenterX=15.5 CenterY=-15.5 CenterZ=0 NormalX=0 NormalY=0 NormalZ=1 AngleXU=0 Radius=1.25
    g1: Circle CenterX=15.5 CenterY=15.5 CenterZ=0 NormalX=0 NormalY=0 NormalZ=1 AngleXU=0 Radius=1.25
    g2: Circle CenterX=-15.5 CenterY=15.5 CenterZ=0 NormalX=0 NormalY=0 NormalZ=1 AngleXU=0 Radius=1.25
    g3: Circle CenterX=-15.5 CenterY=-15.5 CenterZ=0 NormalX=0 NormalY=0 NormalZ=1 AngleXU=0 Radius=1.25
  constraints (9):
    c: Diameter(g0) = 2.5
    c: Symmetric(g1,g0,g-1)
    c: Symmetric(g1,g2,g-2)
    c: Symmetric(g3,g2,g-1)
    c: Equal(g2,g1)
    c: Equal(g1,g3)
    c: Equal(g3,g0)
    c: DistanceX(g2,g1) = 31
    c: DistanceY(g0,g1) = 31
FEATURE [PartDesign::Hole] Hole
  BaseFeature = -> Chamfer
  CustomThreadClearance = 0
  Depth = 4
  DepthType = 0
  Diameter = 3.4
  DrillForDepth = false
  DrillPoint = 1
  DrillPointAngle = 118
  HoleCutCountersinkAngle = 90
  HoleCutCustomValues = false
  HoleCutDepth = 0
  HoleCutDiameter = 1.6
  HoleCutType = 0
  ModelThread = false
  Profile = -> Sketch004
  Tapered = false
  TaperedAngle = 90
  ThreadClass = 0
  ThreadDepth = 4
  ThreadDepthType = 0
  ThreadDirection = 0
  ThreadFit = 0
  ThreadSize = 9
  ThreadType = 1
  Threaded = false
  UseCustomThreadClearance = false
FEATURE [PartDesign::Chamfer] Chamfer001
  Angle = 45
  Base = -> Hole [Edge20,Edge17,Edge22,Edge18]
  BaseFeature = -> Hole
  ChamferType = 0
  FlipDirection = false
  Size = 5
  Size2 = 1
  SupportTransform = true
  UseAllEdges = false
FEATURE [PartDesign::Body] Body  label="nema17"
  Group = -> [Sketch,Pad,Sketch001,Pad001,Sketch002,Pad002,Chamfer,Sketch004,Hole,Chamfer001]
  Origin = -> Origin
  Placement = pos=(0,0,-50) rot=(0,0,1;0rad)
  Tip = -> Chamfer001
FEATURE [App::Part] Part  label="nema17-48"
  Group = -> [Body]
  Origin = -> Origin001
---- part shaft0.FCStd = doc fcstd_3dd2ea7a48e9 ----
FCSTD DOCUMENT  (FreeCAD 2024.1R35694 (Git))
Label: shaft0
License: All rights reserved
LicenseURL: https://en.wikipedia.org/wiki/All_rights_reserved
objects: Sketcher::SketchObject×10, PartDesign::Pocket×5, PartDesign::Revolution×2, PartDesign::Body×2, PartDesign::Chamfer×2, PartDesign::Pad×1, PartDesign::Hole×1, PartDesign::Fillet×1, PartDesign::Groove×1, App::Part×1
note: 38 computed .brp shape members not serialized (recipe doc carries the construction recipe); baked Part::Feature solids carry a one-line shape summary decoded from their .brp

FEATURE [Sketcher::SketchObject] Sketch
  FullyConstrained = true
  MapMode = 5
  Support = -> [XY_Plane001]
  sketch-geometry (8):
    g0: LineSegment StartX=0 StartY=0 StartZ=0 EndX=0 EndY=2.5 EndZ=0
    g1: LineSegment StartX=0 StartY=2.5 StartZ=0 EndX=-119.804 EndY=2.5 EndZ=0
    g2: LineSegment StartX=-119.804 StartY=2.5 StartZ=0 EndX=-125 EndY=5.5 EndZ=0
    g3: LineSegment StartX=-125 StartY=5.5 StartZ=0 EndX=-145 EndY=5.5 EndZ=0
    g4: LineSegment StartX=-145 StartY=5.5 StartZ=0 EndX=-145 EndY=2.5 EndZ=0
    g5: LineSegment StartX=-145 StartY=2.5 StartZ=0 EndX=-130 EndY=2.5 EndZ=0
    g6: LineSegment StartX=-130 StartY=2.5 StartZ=0 EndX=-130 EndY=0 EndZ=0
    g7: LineSegment StartX=-130 StartY=0 StartZ=0 EndX=0 EndY=0 EndZ=0
  constraints (23):
    c: Coincident(g-1,g0)
    c: PointOnObject(g0,g-2)
    c: Coincident(g0,g1)
    c: Horizontal(g1)
    c: Coincident(g1,g2)
    c: Coincident(g2,g3)
    c: Horizontal(g3)
    c: Coincident(g3,g4)
    c: Vertical(g4)
    c: Coincident(g4,g5)
    c: Horizontal(g5)
    c: Coincident(g5,g6)
    c: PointOnObject(g6,g-1)
    c: Vertical(g6)
    c: Coincident(g6,g7)
    c: Coincident(g7,g0)
    c: DistanceY(g-1,g5) = 2.5
    c: DistanceY(g4,g4) = 3
    c: DistanceY(g-1,g0) = 2.5
    c: DistanceX(g3,g3) = 20
    c: DistanceX(g5,g5) = 15
    c: DistanceX(g4,g-1) = 145
    c: Angle(g2,g3) = 0.523599
FEATURE [PartDesign::Revolution] Revolution
  Angle = 360
  Angle2 = 60
  Axis = (1,0,0)
  Base = (0,0,0)
  Profile = -> Sketch
  ReferenceAxis = -> Sketch [H_Axis]
  Refine = true
  Type = 0
FEATURE [Sketcher::SketchObject] Sketch001
  FullyConstrained = true
  MapMode = 5
  Placement = pos=(0,0,0) rot=(0.57735,0.57735,0.57735;2.0944rad)
  Support = -> [Revolution]
  sketch-geometry (8):
    g0: LineSegment StartX=-7.5 StartY=2 StartZ=0 EndX=7.5 EndY=2 EndZ=0
    g1: LineSegment StartX=7.5 StartY=2 StartZ=0 EndX=7.5 EndY=7 EndZ=0
    g2: LineSegment StartX=7.5 StartY=7 StartZ=0 EndX=-7.5 EndY=7 EndZ=0
    g3: LineSegment StartX=-7.5 StartY=7 StartZ=0 EndX=-7.5 EndY=2 EndZ=0
    g4: LineSegment StartX=-7.5 StartY=-7 StartZ=0 EndX=7.5 EndY=-7 EndZ=0
    g5: LineSegment StartX=7.5 StartY=-7 StartZ=0 EndX=7.5 EndY=-2 EndZ=0
    g6: LineSegment StartX=7.5 StartY=-2 StartZ=0 EndX=-7.5 EndY=-2 EndZ=0
    g7: LineSegment StartX=-7.5 StartY=-2 StartZ=0 EndX=-7.5 EndY=-7 EndZ=0
  constraints (21):
    c: Coincident(g0,g1)
    c: Coincident(g1,g2)
    c: Coincident(g2,g3)
    c: Coincident(g3,g0)
    c: Horizontal(g0)
    c: Vertical(g1)
    c: Vertical(g3)
    c: Coincident(g4,g5)
    c: Coincident(g5,g6)
    c: Coincident(g6,g7)
    c: Coincident(g7,g4)
    c: Horizontal(g4)
    c: Vertical(g5)
    c: Vertical(g7)
    c: Symmetric(g5,g0,g-1)
    c: Symmetric(g6,g0,g-1)
    c: Equal(g3,g7)
    c: Symmetric(g2,g1,g-2)
    c: DistanceY(g5,g0) = 4
    c: DistanceY(g5,g5) = 5
    c: DistanceX(g4,g4) = 15
FEATURE [PartDesign::Pocket] Pocket
  BaseFeature = -> Revolution
  Direction = (-1,0,0)
  Length = 7
  Length2 = 5
  Profile = -> Sketch001
  ReferenceAxis = -> Sketch001 [N_Axis]
  Refine = true
  Type = 0
FEATURE [PartDesign::Body] Body  label="shaft0_skel"
  Group = -> [Sketch,Revolution,Sketch001,Pocket]
  Origin = -> Origin001
  Tip = -> Pocket
FEATURE [Sketcher::SketchObject] Sketch002
  FullyConstrained = true
  MapMode = 5
  Support = -> [XY_Plane002]
  sketch-geometry (8):
    g0: LineSegment StartX=0 StartY=0 StartZ=0 EndX=0 EndY=2.5 EndZ=0
    g1: LineSegment StartX=0 StartY=2.5 StartZ=0 EndX=-119.631 EndY=2.5 EndZ=0
    g2: LineSegment StartX=-119.631 StartY=2.5 StartZ=0 EndX=-125 EndY=5.6 EndZ=0
    g3: LineSegment StartX=-125 StartY=5.6 StartZ=0 EndX=-145 EndY=5.6 EndZ=0
    g4: LineSegment StartX=-145 StartY=5.6 StartZ=0 EndX=-145 EndY=2.6 EndZ=0
    g5: LineSegment StartX=-145 StartY=2.6 StartZ=0 EndX=-130 EndY=2.6 EndZ=0
    g6: LineSegment StartX=-130 StartY=2.6 StartZ=0 EndX=-130 EndY=0 EndZ=0
    g7: LineSegment StartX=-130 StartY=0 StartZ=0 EndX=0 EndY=0 EndZ=0
  constraints (23):
    c: Coincident(g-1,g0)
    c: PointOnObject(g0,g-2)
    c: Coincident(g0,g1)
    c: Horizontal(g1)
    c: Coincident(g1,g2)
    c: Coincident(g2,g3)
    c: Horizontal(g3)
    c: Coincident(g3,g4)
    c: Vertical(g4)
    c: Coincident(g4,g5)
    c: Horizontal(g5)
    c: Coincident(g5,g6)
    c: PointOnObject(g6,g-1)
    c: Vertical(g6)
    c: Coincident(g6,g7)
    c: Coincident(g7,g0)
    c: DistanceY(g-1,g5) = 2.6
    c: DistanceY(g4,g4) = 3
    c: DistanceY(g-1,g0) = 2.5
    c: DistanceX(g3,g3) = 20
    c: DistanceX(g5,g5) = 15
    c: DistanceX(g4,g-1) = 145
    c: Angle(g2,g3) = 0.523599
FEATURE [PartDesign::Revolution] Revolution001
  Angle = 360
  Angle2 = 60
  Axis = (1,0,0)
  Base = (0,0,0)
  Profile = -> Sketch002
  ReferenceAxis = -> Sketch002 [H_Axis]
  Refine = true
  Type = 0
FEATURE [Sketcher::SketchObject] Sketch003
  FullyConstrained = true
  MapMode = 5
  Placement = pos=(0,0,0) rot=(0.57735,0.57735,0.57735;2.0944rad)
  Support = -> [Revolution001]
  sketch-geometry (8):
    g0: LineSegment StartX=-7.5 StartY=1.9 StartZ=0 EndX=7.5 EndY=1.9 EndZ=0
    g1: LineSegment StartX=7.5 StartY=1.9 StartZ=0 EndX=7.5 EndY=6.9 EndZ=0
    g2: LineSegment StartX=7.5 StartY=6.9 StartZ=0 EndX=-7.5 EndY=6.9 EndZ=0
    g3: LineSegment StartX=-7.5 StartY=6.9 StartZ=0 EndX=-7.5 EndY=1.9 EndZ=0
    g4: LineSegment StartX=-7.5 StartY=-6.9 StartZ=0 EndX=7.5 EndY=-6.9 EndZ=0
    g5: LineSegment StartX=7.5 StartY=-6.9 StartZ=0 EndX=7.5 EndY=-1.9 EndZ=0
    g6: LineSegment StartX=7.5 StartY=-1.9 StartZ=0 EndX=-7.5 EndY=-1.9 EndZ=0
    g7: LineSegment StartX=-7.5 StartY=-1.9 StartZ=0 EndX=-7.5 EndY=-6.9 EndZ=0
  constraints (21):
    c: Coincident(g0,g1)
    c: Coincident(g1,g2)
    c: Coincident(g2,g3)
    c: Coincident(g3,g0)
    c: Horizontal(g0)
    c: Vertical(g1)
    c: Vertical(g3)
    c: Coincident(g4,g5)
    c: Coincident(g5,g6)
    c: Coincident(g6,g7)
    c: Coincident(g7,g4)
    c: Horizontal(g4)
    c: Vertical(g5)
    c: Vertical(g7)
    c: Symmetric(g5,g0,g-1)
    c: Symmetric(g6,g0,g-1)
    c: Equal(g3,g7)
    c: Symmetric(g2,g1,g-2)
    c: DistanceY(g5,g0) = 3.8
    c: DistanceY(g5,g5) = 5
    c: DistanceX(g4,g4) = 15
FEATURE [PartDesign::Pocket] Pocket001
  BaseFeature = -> Revolution001
  Direction = (-1,0,0)
  Length = 7
  Length2 = 5
  Profile = -> Sketch003
  ReferenceAxis = -> Sketch003 [N_Axis]
  Refine = true
  Type = 0
FEATURE [PartDesign::Chamfer] Chamfer
  Angle = 15
  Base = -> Pocket001 [Edge20]
  BaseFeature = -> Pocket001
  ChamferType = 2
  FlipDirection = true
  Refine = true
  Size = 2
  Size2 = 1
  SupportTransform = false
  UseAllEdges = false
FEATURE [Sketcher::SketchObject] Sketch004
  ExternalGeometry = -> [Chamfer]
  FullyConstrained = true
  MapMode = 5
  Placement = pos=(-145,0,0) rot=(0.57735,-0.57735,-0.57735;2.0944rad)
  Support = -> [Chamfer]
  sketch-geometry (4):
    g0: ArcOfCircle CenterX=0 CenterY=0 CenterZ=0 NormalX=0 NormalY=0 NormalZ=1 AngleXU=0 Radius=5.6 StartAngle=0.189265 EndAngle=2.95233
    g1: LineSegment StartX=-5.5 StartY=1.05357 StartZ=0 EndX=-5.5 EndY=9 EndZ=0
    g2: LineSegment StartX=-5.5 StartY=9 StartZ=0 EndX=5.5 EndY=9 EndZ=0
    g3: LineSegment StartX=5.5 StartY=9 StartZ=0 EndX=5.5 EndY=1.05357 EndZ=0
  constraints (11):
    c: Coincident(g0,g-3)
    c: Vertical(g1)
    c: Coincident(g1,g2)
    c: Coincident(g2,g3)
    c: Vertical(g3)
    c: Symmetric(g1,g2,g-2)
    c: Coincident(g0,g1)
    c: Coincident(g0,g3)
    c: Equal(g0,g-3)
    c: DistanceX(g2,g2) = 11
    c: DistanceY(g-1,g2) = 9
FEATURE [PartDesign::Pad] Pad
  BaseFeature = -> Chamfer
  Direction = (-1,0,0)
  Length = 10
  Length2 = 10
  Profile = -> Sketch004
  ReferenceAxis = -> Sketch004 [N_Axis]
  Refine = true
  Reversed = true
  Type = 0
FEATURE [Sketcher::SketchObject] Sketch005
  ExternalGeometry = -> [Pad]
  FullyConstrained = true
  MapMode = 5
  Placement = pos=(0,-5.5,0) rot=(1,0,0;1.5708rad)
  Support = -> [Pad]
  sketch-geometry (1):
    g0: Circle CenterX=-140 CenterY=5 CenterZ=0 NormalX=0 NormalY=0 NormalZ=1 AngleXU=0 Radius=1.5
  constraints (3):
    c: DistanceX(g-3,g0) = 5
    c: DistanceY(g-1,g0) = 5
    c: Diameter(g0) = 3
FEATURE [PartDesign::Hole] Hole
  BaseFeature = -> Pad
  CustomThreadClearance = 0
  Depth = 25
  DepthType = 0
  Diameter = 3.4
  DrillForDepth = false
  DrillPoint = 1
  DrillPointAngle = 118
  HoleCutCountersinkAngle = 90
  HoleCutCustomValues = false
  HoleCutDepth = 2
  HoleCutDiameter = 6.1
  HoleCutType = 1
  ModelThread = false
  Profile = -> Sketch005
  Refine = true
  Tapered = false
  TaperedAngle = 90
  ThreadClass = 0
  ThreadDepth = 25
  ThreadDepthType = 0
  ThreadDirection = 0
  ThreadFit = 0
  ThreadSize = 9
  ThreadType = 1
  Threaded = false
  UseCustomThreadClearance = false
FEATURE [Sketcher::SketchObject] Sketch006
  ExternalGeometry = -> [Hole]
  FullyConstrained = true
  MapMode = 5
  Placement = pos=(0,5.5,0) rot=(0,0.707107,0.707107;3.14159rad)
  Support = -> [Hole]
  sketch-geometry (7):
    g0: LineSegment StartX=143.522 StartY=5 StartZ=0 EndX=141.761 EndY=8.05 EndZ=0
    g1: LineSegment StartX=141.761 StartY=8.05 StartZ=0 EndX=138.239 EndY=8.05 EndZ=0
    g2: LineSegment StartX=138.239 StartY=8.05 StartZ=0 EndX=136.478 EndY=5 EndZ=0
    g3: LineSegment StartX=136.478 StartY=5 StartZ=0 EndX=138.239 EndY=1.95 EndZ=0
    g4: LineSegment StartX=138.239 StartY=1.95 StartZ=0 EndX=141.761 EndY=1.95 EndZ=0
    g5: LineSegment StartX=141.761 StartY=1.95 StartZ=0 EndX=143.522 EndY=5 EndZ=0
    g6: Circle CenterX=140 CenterY=5 CenterZ=0 NormalX=0 NormalY=0 NormalZ=1 AngleXU=0 Radius=3.52184
  constraints (16):
    c: Coincident(g0,g1)
    c: Coincident(g1,g2)
    c: Coincident(g2,g3)
    c: Coincident(g3,g4)
    c: Coincident(g4,g5)
    c: Coincident(g5,g0)
    c: Equal(g0, g1-g5) x5
    c: PointOnObject(g0,g6)
    c: PointOnObject(g1,g6)
    c: PointOnObject(g2,g6)
    c: PointOnObject(g3,g6)
    c: PointOnObject(g4,g6)
    c: PointOnObject(g5,g6)
    c: Coincident(g6,g-3)
    c: DistanceY(g4,g0) = 6.1
    c: Horizontal(g4)
FEATURE [PartDesign::Pocket] Pocket002
  BaseFeature = -> Hole
  Direction = (0,-1,2e-16)
  Length = 3
  Length2 = 5
  Profile = -> Sketch006
  ReferenceAxis = -> Sketch006 [N_Axis]
  Refine = true
  Type = 0
FEATURE [Sketcher::SketchObject] Sketch007
  FullyConstrained = true
  MapMode = 5
  Placement = pos=(0,0,0) rot=(0.57735,0.57735,0.57735;2.0944rad)
  Support = -> [Pocket002]
  sketch-geometry (2):
    g0: Circle CenterX=0 CenterY=0 CenterZ=0 NormalX=0 NormalY=0 NormalZ=1 AngleXU=0 Radius=2.45
    g1: Circle CenterX=0 CenterY=0 CenterZ=0 NormalX=0 NormalY=0 NormalZ=1 AngleXU=0 Radius=5
  constraints (4):
    c: Coincident(g1,g0)
    c: Diameter(g0) = 4.9
    c: Diameter(g1) = 10
    c: Coincident(g0,g-1)
FEATURE [PartDesign::Pocket] Pocket003
  BaseFeature = -> Pocket002
  Direction = (-1,0,0)
  Length = 0
  Length2 = 5
  Profile = -> Sketch007
  ReferenceAxis = -> Sketch007 [N_Axis]
  Refine = true
  Type = 3
  UpToFace = -> Pocket002 [Face24]
FEATURE [PartDesign::Fillet] Fillet
  Base = -> Pocket003
  BaseFeature = -> Pocket003
  Radius = 3
  Refine = true
  SupportTransform = false
  UseAllEdges = false
FEATURE [Sketcher::SketchObject] Sketch008
  FullyConstrained = true
  MapMode = 5
  Placement = pos=(-145,0,0) rot=(0.57735,-0.57735,-0.57735;2.0944rad)
  Support = -> [Fillet]
  sketch-geometry (4):
    g0: LineSegment StartX=1 StartY=0 StartZ=0 EndX=1 EndY=15 EndZ=0
    g1: LineSegment StartX=1 StartY=15 StartZ=0 EndX=-1 EndY=15 EndZ=0
    g2: LineSegment StartX=-1 StartY=15 StartZ=0 EndX=-1 EndY=0 EndZ=0
    g3: LineSegment StartX=-1 StartY=0 StartZ=0 EndX=1 EndY=0 EndZ=0
  constraints (11):
    c: Coincident(g0,g1)
    c: Coincident(g1,g2)
    c: Coincident(g2,g3)
    c: Coincident(g3,g0)
    c: Vertical(g0)
    c: Vertical(g2)
    c: Horizontal(g3)
    c: PointOnObject(g0,g-1)
    c: Symmetric(g1,g0,g-2)
    c: DistanceX(g1,g1) = 2
    c: DistanceY(g0,g0) = 15
FEATURE [PartDesign::Pocket] Pocket004
  BaseFeature = -> Fillet
  Direction = (1,0,0)
  Length = 15
  Length2 = 5
  Profile = -> Sketch008
  ReferenceAxis = -> Sketch008 [N_Axis]
  Refine = true
  Type = 0
FEATURE [PartDesign::Chamfer] Chamfer001
  Angle = 45
  Base = -> Pocket004 [Edge86,Edge87,Edge85,Edge81,Edge84]
  BaseFeature = -> Pocket004
  ChamferType = 0
  FlipDirection = false
  Refine = true
  Size = 0.2
  Size2 = 1
  SupportTransform = false
  UseAllEdges = false
FEATURE [Sketcher::SketchObject] Sketch009
  ExternalGeometry = -> [Chamfer001]
  FullyConstrained = true
  MapMode = 5
  Support = -> [XY_Plane002]
  sketch-geometry (4):
    g0: LineSegment StartX=-7 StartY=3.3 StartZ=0 EndX=-7 EndY=2.3 EndZ=0
    g1: LineSegment StartX=-7 StartY=2.3 StartZ=0 EndX=-4 EndY=2.3 EndZ=0
    g2: LineSegment StartX=-4 StartY=2.3 StartZ=0 EndX=-4 EndY=3.3 EndZ=0
    g3: LineSegment StartX=-4 StartY=3.3 StartZ=0 EndX=-7 EndY=3.3 EndZ=0
  constraints (12):
    c: Coincident(g0,g1)
    c: Coincident(g1,g2)
    c: Coincident(g2,g3)
    c: Coincident(g3,g0)
    c: Vertical(g0)
    c: Vertical(g2)
    c: Horizontal(g1)
    c: Horizontal(g3)
    c: PointOnObject(g-3,g0)
    c: DistanceY(g-1,g1) = 2.3
    c: DistanceX(g3,g3) = 3
    c: DistanceY(g2,g2) = 1
FEATURE [PartDesign::Groove] Groove
  Angle = 360
  Angle2 = 60
  Axis = (1,0,0)
  Base = (0,0,0)
  BaseFeature = -> Chamfer001
  Profile = -> Sketch009
  ReferenceAxis = -> Sketch009 [H_Axis]
  Refine = true
  Reversed = true
  Type = 0
FEATURE [PartDesign::Body] Body001  label="shaft0s"
  Group = -> [Sketch002,Revolution001,Sketch003,Pocket001,Chamfer,Sketch004,Pad,Sketch005,Hole,Sketch006,Pocket002,Sketch007,Pocket003,Fillet,Sketch008,Pocket004,Chamfer001,Sketch009,Groove]
  Origin = -> Origin002
  Tip = -> Groove
FEATURE [App::Part] Part  label="shaft0"
  Group = -> [Body,Body001]
  Origin = -> Origin
---- part shaft1.FCStd = doc fcstd_a6ef72078356 ----
FCSTD DOCUMENT  (FreeCAD 2024.1R35694 (Git))
Label: shaft1
License: All rights reserved
LicenseURL: https://en.wikipedia.org/wiki/All_rights_reserved
objects: Sketcher::SketchObject×7, PartDesign::Pocket×5, PartDesign::Revolution×2, PartDesign::Body×2, PartDesign::Chamfer×1, PartDesign::Plane×1, App::Part×1
note: 26 computed .brp shape members not serialized (recipe doc carries the construction recipe); baked Part::Feature solids carry a one-line shape summary decoded from their .brp

FEATURE [Sketcher::SketchObject] Sketch
  FullyConstrained = true
  MapMode = 5
  Support = -> [XY_Plane001]
  sketch-geometry (8):
    g0: LineSegment StartX=7 StartY=0 StartZ=0 EndX=7 EndY=2.5 EndZ=0
    g1: LineSegment StartX=7 StartY=2.5 StartZ=0 EndX=0 EndY=2.5 EndZ=0
    g2: LineSegment StartX=0 StartY=2.5 StartZ=0 EndX=0 EndY=3 EndZ=0
    g3: LineSegment StartX=0 StartY=3 StartZ=0 EndX=-4 EndY=3 EndZ=0
    g4: LineSegment StartX=-4 StartY=3 StartZ=0 EndX=-4 EndY=2.5 EndZ=0
    g5: LineSegment StartX=-4 StartY=2.5 StartZ=0 EndX=-19 EndY=2.5 EndZ=0
    g6: LineSegment StartX=-19 StartY=2.5 StartZ=0 EndX=-19 EndY=0 EndZ=0
    g7: LineSegment StartX=-19 StartY=0 StartZ=0 EndX=7 EndY=0 EndZ=0
  constraints (24):
    c: PointOnObject(g0,g-1)
    c: Vertical(g0)
    c: Coincident(g0,g1)
    c: PointOnObject(g1,g-2)
    c: Horizontal(g1)
    c: Coincident(g1,g2)
    c: PointOnObject(g2,g-2)
    c: Coincident(g2,g3)
    c: Horizontal(g3)
    c: Coincident(g3,g4)
    c: Coincident(g4,g5)
    c: Horizontal(g5)
    c: Coincident(g5,g6)
    c: PointOnObject(g6,g-1)
    c: Coincident(g6,g7)
    c: Coincident(g7,g0)
    c: Vertical(g6)
    c: Vertical(g4)
    c: DistanceY(g-1,g0) = 2.5
    c: DistanceY(g-1,g2) = 3
    c: DistanceY(g6,g6) = 2.5
    c: DistanceX(g1,g1) = 7
    c: DistanceX(g3,g3) = 4
    c: DistanceX(g5,g5) = 15
FEATURE [PartDesign::Revolution] Revolution
  Angle = 360
  Angle2 = 60
  Axis = (1,0,0)
  Base = (0,0,0)
  Profile = -> Sketch
  ReferenceAxis = -> Sketch [H_Axis]
  Refine = true
  Type = 0
FEATURE [Sketcher::SketchObject] Sketch001
  FullyConstrained = true
  MapMode = 5
  Placement = pos=(-19,0,0) rot=(0.57735,-0.57735,-0.57735;2.0944rad)
  Support = -> [Revolution]
  sketch-geometry (8):
    g0: LineSegment StartX=-5 StartY=7 StartZ=0 EndX=-5 EndY=2 EndZ=0
    g1: LineSegment StartX=-5 StartY=2 StartZ=0 EndX=5 EndY=2 EndZ=0
    g2: LineSegment StartX=5 StartY=2 StartZ=0 EndX=5 EndY=7 EndZ=0
    g3: LineSegment StartX=5 StartY=7 StartZ=0 EndX=-5 EndY=7 EndZ=0
    g4: LineSegment StartX=-5 StartY=-7 StartZ=0 EndX=5 EndY=-7 EndZ=0
    g5: LineSegment StartX=5 StartY=-7 StartZ=0 EndX=5 EndY=-2 EndZ=0
    g6: LineSegment StartX=5 StartY=-2 StartZ=0 EndX=-5 EndY=-2 EndZ=0
    g7: LineSegment StartX=-5 StartY=-2 StartZ=0 EndX=-5 EndY=-7 EndZ=0
  constraints (21):
    c: Coincident(g0,g1)
    c: Coincident(g1,g2)
    c: Coincident(g2,g3)
    c: Coincident(g3,g0)
    c: Vertical(g0)
    c: Vertical(g2)
    c: Horizontal(g3)
    c: Coincident(g4,g5)
    c: Coincident(g5,g6)
    c: Coincident(g6,g7)
    c: Coincident(g7,g4)
    c: Horizontal(g4)
    c: Vertical(g5)
    c: Vertical(g7)
    c: Symmetric(g1,g5,g-1)
    c: Symmetric(g0,g1,g-2)
    c: Symmetric(g6,g0,g-1)
    c: Equal(g2,g5)
    c: DistanceY(g5,g1) = 4
    c: DistanceY(g2,g2) = 5
    c: DistanceX(g3,g3) = 10
FEATURE [PartDesign::Pocket] Pocket
  BaseFeature = -> Revolution
  Direction = (1,0,0)
  Length = 5
  Length2 = 5
  Profile = -> Sketch001
  ReferenceAxis = -> Sketch001 [N_Axis]
  Refine = true
  Type = 0
FEATURE [Sketcher::SketchObject] Sketch002
  FullyConstrained = true
  MapMode = 5
  Placement = pos=(7,0,0) rot=(0.57735,0.57735,0.57735;2.0944rad)
  Support = -> [Pocket]
  sketch-geometry (8):
    g0: LineSegment StartX=-5 StartY=2 StartZ=0 EndX=5 EndY=2 EndZ=0
    g1: LineSegment StartX=5 StartY=2 StartZ=0 EndX=5 EndY=7 EndZ=0
    g2: LineSegment StartX=5 StartY=7 StartZ=0 EndX=-5 EndY=7 EndZ=0
    g3: LineSegment StartX=-5 StartY=7 StartZ=0 EndX=-5 EndY=2 EndZ=0
    g4: LineSegment StartX=-5 StartY=-7 StartZ=0 EndX=5 EndY=-7 EndZ=0
    g5: LineSegment StartX=5 StartY=-7 StartZ=0 EndX=5 EndY=-2 EndZ=0
    g6: LineSegment StartX=5 StartY=-2 StartZ=0 EndX=-5 EndY=-2 EndZ=0
    g7: LineSegment StartX=-5 StartY=-2 StartZ=0 EndX=-5 EndY=-7 EndZ=0
  constraints (21):
    c: Coincident(g0,g1)
    c: Coincident(g1,g2)
    c: Coincident(g2,g3)
    c: Coincident(g3,g0)
    c: Horizontal(g0)
    c: Vertical(g1)
    c: Vertical(g3)
    c: Coincident(g4,g5)
    c: Coincident(g5,g6)
    c: Coincident(g6,g7)
    c: Coincident(g7,g4)
    c: Horizontal(g4)
    c: Vertical(g5)
    c: Vertical(g7)
    c: Symmetric(g0,g6,g-1)
    c: Symmetric(g0,g5,g-1)
    c: Symmetric(g2,g1,g-2)
    c: Equal(g1,g5)
    c: DistanceY(g5,g0) = 4
    c: DistanceY(g1,g1) = 5
    c: DistanceX(g2,g2) = 10
FEATURE [PartDesign::Pocket] Pocket001
  BaseFeature = -> Pocket
  Direction = (-1,0,0)
  Length = 7
  Length2 = 5
  Profile = -> Sketch002
  ReferenceAxis = -> Sketch002 [N_Axis]
  Refine = true
  Type = 0
FEATURE [PartDesign::Body] Body  label="shaft1_skel"
  Group = -> [Sketch,Revolution,Sketch001,Pocket,Sketch002,Pocket001]
  Origin = -> Origin001
  Tip = -> Pocket001
FEATURE [Sketcher::SketchObject] Sketch003
  FullyConstrained = true
  MapMode = 5
  Support = -> [XY_Plane002]
  sketch-geometry (8):
    g0: LineSegment StartX=7 StartY=0 StartZ=0 EndX=7 EndY=2.45 EndZ=0
    g1: LineSegment StartX=7 StartY=2.45 StartZ=0 EndX=0 EndY=2.45 EndZ=0
    g2: LineSegment StartX=0 StartY=2.45 StartZ=0 EndX=0 EndY=3 EndZ=0
    g3: LineSegment StartX=0 StartY=3 StartZ=0 EndX=-4 EndY=3 EndZ=0
    g4: LineSegment StartX=-4 StartY=3 StartZ=0 EndX=-4 EndY=2.5 EndZ=0
    g5: LineSegment StartX=-4 StartY=2.5 StartZ=0 EndX=-19 EndY=2.5 EndZ=0
    g6: LineSegment StartX=-19 StartY=2.5 StartZ=0 EndX=-19 EndY=0 EndZ=0
    g7: LineSegment StartX=-19 StartY=0 StartZ=0 EndX=7 EndY=0 EndZ=0
  constraints (24):
    c: PointOnObject(g0,g-1)
    c: Vertical(g0)
    c: Coincident(g0,g1)
    c: PointOnObject(g1,g-2)
    c: Horizontal(g1)
    c: Coincident(g1,g2)
    c: PointOnObject(g2,g-2)
    c: Coincident(g2,g3)
    c: Horizontal(g3)
    c: Coincident(g3,g4)
    c: Coincident(g4,g5)
    c: Horizontal(g5)
    c: Coincident(g5,g6)
    c: PointOnObject(g6,g-1)
    c: Coincident(g6,g7)
    c: Coincident(g7,g0)
    c: Vertical(g6)
    c: Vertical(g4)
    c: DistanceY(g-1,g0) = 2.45
    c: DistanceY(g-1,g2) = 3
    c: DistanceY(g6,g6) = 2.5
    c: DistanceX(g1,g1) = 7
    c: DistanceX(g3,g3) = 4
    c: DistanceX(g5,g5) = 15
FEATURE [PartDesign::Revolution] Revolution001
  Angle = 360
  Angle2 = 60
  Axis = (1,0,0)
  Base = (0,0,0)
  Profile = -> Sketch003
  ReferenceAxis = -> Sketch003 [H_Axis]
  Refine = true
  Type = 0
FEATURE [Sketcher::SketchObject] Sketch004
  FullyConstrained = true
  MapMode = 5
  Placement = pos=(-19,0,0) rot=(0.57735,-0.57735,-0.57735;2.0944rad)
  Support = -> [Revolution001]
  sketch-geometry (8):
    g0: LineSegment StartX=-5 StartY=6.9 StartZ=0 EndX=-5 EndY=1.9 EndZ=0
    g1: LineSegment StartX=-5 StartY=1.9 StartZ=0 EndX=5 EndY=1.9 EndZ=0
    g2: LineSegment StartX=5 StartY=1.9 StartZ=0 EndX=5 EndY=6.9 EndZ=0
    g3: LineSegment StartX=5 StartY=6.9 StartZ=0 EndX=-5 EndY=6.9 EndZ=0
    g4: LineSegment StartX=-5 StartY=-6.9 StartZ=0 EndX=5 EndY=-6.9 EndZ=0
    g5: LineSegment StartX=5 StartY=-6.9 StartZ=0 EndX=5 EndY=-1.9 EndZ=0
    g6: LineSegment StartX=5 StartY=-1.9 StartZ=0 EndX=-5 EndY=-1.9 EndZ=0
    g7: LineSegment StartX=-5 StartY=-1.9 StartZ=0 EndX=-5 EndY=-6.9 EndZ=0
  constraints (21):
    c: Coincident(g0,g1)
    c: Coincident(g1,g2)
    c: Coincident(g2,g3)
    c: Coincident(g3,g0)
    c: Vertical(g0)
    c: Vertical(g2)
    c: Horizontal(g3)
    c: Coincident(g4,g5)
    c: Coincident(g5,g6)
    c: Coincident(g6,g7)
    c: Coincident(g7,g4)
    c: Horizontal(g4)
    c: Vertical(g5)
    c: Vertical(g7)
    c: Symmetric(g1,g5,g-1)
    c: Symmetric(g0,g1,g-2)
    c: Symmetric(g6,g0,g-1)
    c: Equal(g2,g5)
    c: DistanceY(g5,g1) = 3.8
    c: DistanceY(g2,g2) = 5
    c: DistanceX(g3,g3) = 10
FEATURE [PartDesign::Pocket] Pocket002
  BaseFeature = -> Revolution001
  Direction = (1,0,0)
  Length = 5
  Length2 = 5
  Profile = -> Sketch004
  ReferenceAxis = -> Sketch004 [N_Axis]
  Refine = true
  Type = 0
FEATURE [Sketcher::SketchObject] Sketch005
  FullyConstrained = true
  MapMode = 5
  Placement = pos=(7,0,0) rot=(0.57735,0.57735,0.57735;2.0944rad)
  Support = -> [Pocket002]
  sketch-geometry (8):
    g0: LineSegment StartX=-5 StartY=1.9 StartZ=0 EndX=5 EndY=1.9 EndZ=0
    g1: LineSegment StartX=5 StartY=1.9 StartZ=0 EndX=5 EndY=6.9 EndZ=0
    g2: LineSegment StartX=5 StartY=6.9 StartZ=0 EndX=-5 EndY=6.9 EndZ=0
    g3: LineSegment StartX=-5 StartY=6.9 StartZ=0 EndX=-5 EndY=1.9 EndZ=0
    g4: LineSegment StartX=-5 StartY=-6.9 StartZ=0 EndX=5 EndY=-6.9 EndZ=0
    g5: LineSegment StartX=5 StartY=-6.9 StartZ=0 EndX=5 EndY=-1.9 EndZ=0
    g6: LineSegment StartX=5 StartY=-1.9 StartZ=0 EndX=-5 EndY=-1.9 EndZ=0
    g7: LineSegment StartX=-5 StartY=-1.9 StartZ=0 EndX=-5 EndY=-6.9 EndZ=0
  constraints (21):
    c: Coincident(g0,g1)
    c: Coincident(g1,g2)
    c: Coincident(g2,g3)
    c: Coincident(g3,g0)
    c: Horizontal(g0)
    c: Vertical(g1)
    c: Vertical(g3)
    c: Coincident(g4,g5)
    c: Coincident(g5,g6)
    c: Coincident(g6,g7)
    c: Coincident(g7,g4)
    c: Horizontal(g4)
    c: Vertical(g5)
    c: Vertical(g7)
    c: Symmetric(g0,g6,g-1)
    c: Symmetric(g0,g5,g-1)
    c: Symmetric(g2,g1,g-2)
    c: Equal(g1,g5)
    c: DistanceY(g5,g0) = 3.8
    c: DistanceY(g1,g1) = 5
    c: DistanceX(g2,g2) = 10
FEATURE [PartDesign::Pocket] Pocket003
  BaseFeature = -> Pocket002
  Direction = (-1,0,0)
  Length = 7
  Length2 = 5
  Profile = -> Sketch005
  ReferenceAxis = -> Sketch005 [N_Axis]
  Refine = true
  Type = 0
FEATURE [PartDesign::Chamfer] Chamfer
  Angle = 15
  Base = -> Pocket003 [Edge30,Edge28,Edge32,Edge29,Edge31,Edge19,Edge18,Edge10,Edge14,Edge20]
  BaseFeature = -> Pocket003
  ChamferType = 0
  FlipDirection = false
  Refine = true
  Size = 0.4
  Size2 = 0.2
  SupportTransform = false
  UseAllEdges = false
FEATURE [PartDesign::Plane] DatumPlane
  Length = 60
  MapMode = 5
  Placement = pos=(-14,0,0) rot=(0.57735,-0.57735,-0.57735;2.0944rad)
  ResizeMode = 0
  Support = -> [Chamfer]
  Width = 60
FEATURE [Sketcher::SketchObject] Sketch006
  FullyConstrained = true
  MapMode = 5
  Placement = pos=(-14,0,0) rot=(0.57735,-0.57735,-0.57735;2.0944rad)
  Support = -> [DatumPlane]
  sketch-geometry (2):
    g0: Circle CenterX=0 CenterY=0 CenterZ=0 NormalX=0 NormalY=0 NormalZ=1 AngleXU=0 Radius=2.45
    g1: Circle CenterX=0 CenterY=0 CenterZ=0 NormalX=0 NormalY=0 NormalZ=1 AngleXU=0 Radius=3
  constraints (4):
    c: Coincident(g0,g-1)
    c: Coincident(g1,g0)
    c: Diameter(g0) = 4.9
    c: Diameter(g1) = 6
FEATURE [PartDesign::Pocket] Pocket004
  BaseFeature = -> Chamfer
  Direction = (1,0,0)
  Length = 5
  Length2 = 5
  Profile = -> Sketch006
  ReferenceAxis = -> Sketch006 [N_Axis]
  Refine = true
  Reversed = true
  Type = 1
FEATURE [PartDesign::Body] Body001  label="shaft1s"
  Group = -> [Sketch003,Revolution001,Sketch004,Pocket002,Sketch005,Pocket003,Chamfer,DatumPlane,Sketch006,Pocket004]
  Origin = -> Origin002
  Tip = -> Pocket004
FEATURE [App::Part] Part  label="shaft1"
  Group = -> [Body,Body001]
  Origin = -> Origin
